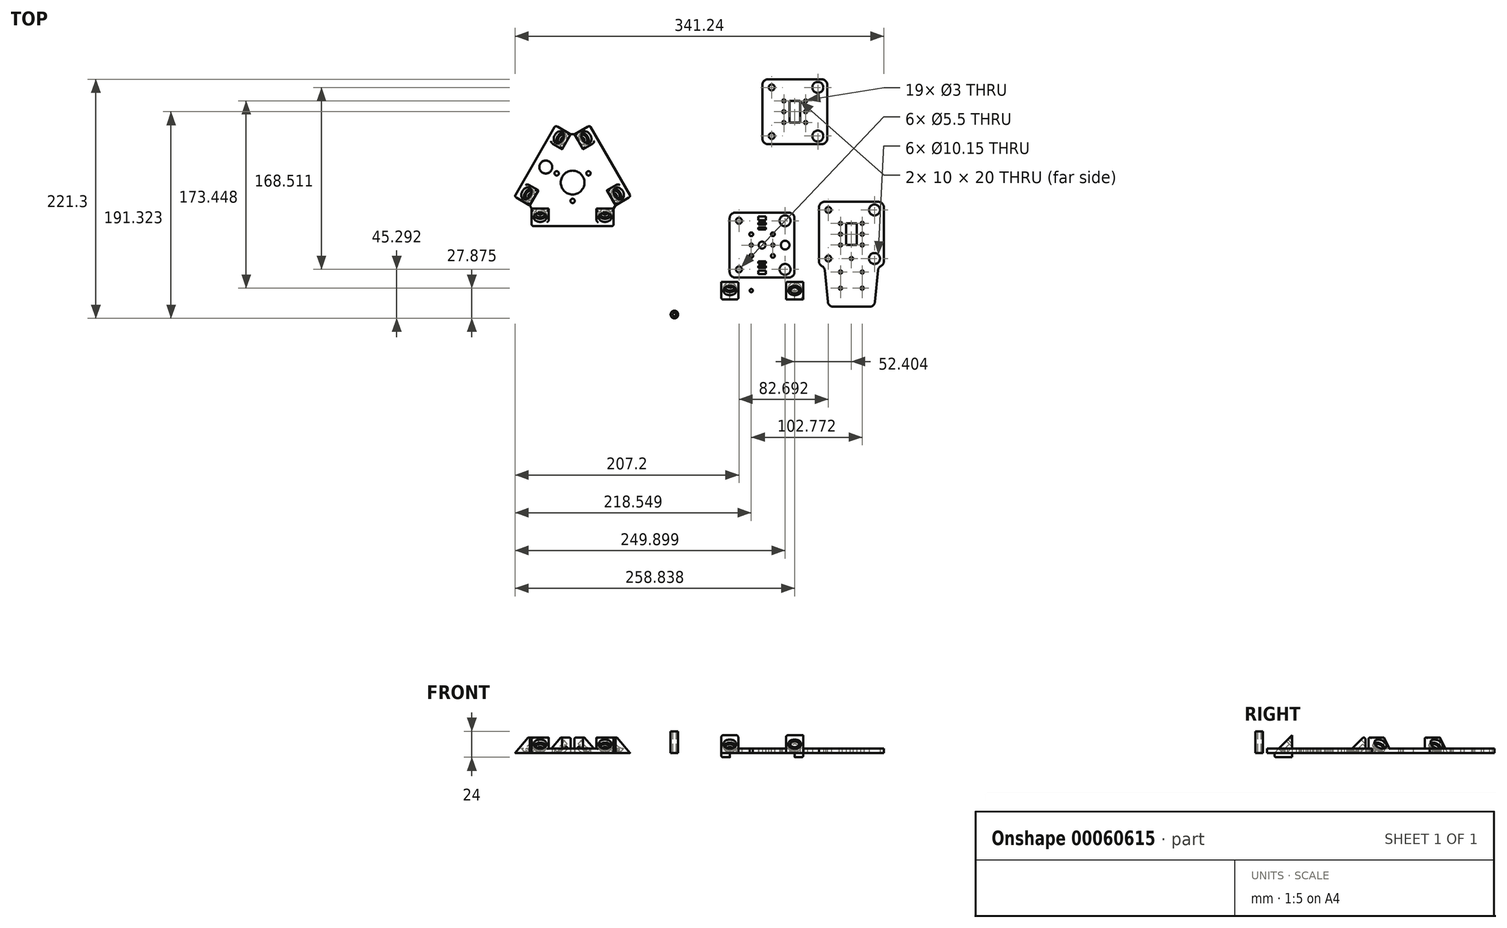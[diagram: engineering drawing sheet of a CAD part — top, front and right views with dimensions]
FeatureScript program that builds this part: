
annotation { "Feature Type Name" : "Feature", "Feature Type Description" : "" }
export const myFeature = defineFeature(function(context is Context, id is Id, definition is map)
    precondition{}
    {
        {
            var Q0;
            Q0=qCreatedBy(makeId("Top.planeOp"),FACE);
            var sketch = newSketch(context, id + "F0", { "sketchPlane" : qUnion([Q0])});
            skArc(sketch, "E0", {"start": v(24.79, -19.87) * mm, "mid": v(28.33, -18.4) * mm, "end": v(29.79, -14.87) * mm});
            skLineSegment(sketch, "E1", {"start": v(24.79, -19.87) * mm, "end": v(-25.21, -19.87) * mm});
            skArc(sketch, "E2", {"start": v(29.79, 35.13) * mm, "mid": v(28.33, 38.67) * mm, "end": v(24.79, 40.13) * mm});
            skLineSegment(sketch, "E3", {"start": v(29.79, 35.13) * mm, "end": v(29.79, -14.87) * mm});
            skArc(sketch, "E4", {"start": v(-25.21, 40.13) * mm, "mid": v(-28.75, 38.67) * mm, "end": v(-30.21, 35.13) * mm});
            skLineSegment(sketch, "E5", {"start": v(-25.21, 40.13) * mm, "end": v(24.79, 40.13) * mm});
            skArc(sketch, "E6", {"start": v(-30.21, -14.87) * mm, "mid": v(-28.75, -18.4) * mm, "end": v(-25.21, -19.87) * mm});
            skLineSegment(sketch, "E7", {"start": v(-30.21, -14.87) * mm, "end": v(-30.21, 35.13) * mm});
            skCircle(sketch, "E8", {"center": v(30, -32.16) * mm, "radius": 5.9 * mm, "construction": true});
            skCircle(sketch, "E9", {"center": v(-30, -32.16) * mm, "radius": 5.9 * mm, "construction": true});
            skLineSegment(sketch, "E10", {"start": v(-30.85, -40.13) * mm, "end": v(30.85, -40.13) * mm});
            skLineSegment(sketch, "E11", {"start": v(30.85, -23.83) * mm, "end": v(-30.85, -23.83) * mm});
            skCircle(sketch, "E12", {"center": v(21.14, 32.63) * mm, "radius": 5.08 * mm});
            skCircle(sketch, "E13", {"center": v(21.14, -12.37) * mm, "radius": 5.08 * mm});
            skCircle(sketch, "E14", {"center": v(-21.56, 32.63) * mm, "radius": 2.75 * mm});
            skCircle(sketch, "E15", {"center": v(-21.56, -12.37) * mm, "radius": 2.75 * mm});
            skCircle(sketch, "E16", {"center": v(-10.21, 20.13) * mm, "radius": 1.75 * mm});
            skCircle(sketch, "E17", {"center": v(-10.21, 0.13) * mm, "radius": 1.75 * mm});
            skCircle(sketch, "E18", {"center": v(9.79, 0.13) * mm, "radius": 1.75 * mm});
            skCircle(sketch, "E19", {"center": v(9.79, 20.13) * mm, "radius": 1.75 * mm});
            skLineSegment(sketch, "E20", {"start": v(-3.63, -6.88) * mm, "end": v(3.37, -6.88) * mm});
            skLineSegment(sketch, "E21", {"start": v(3.37, -6.88) * mm, "end": v(3.37, -4.88) * mm});
            skLineSegment(sketch, "E22", {"start": v(3.37, -4.88) * mm, "end": v(-3.63, -4.88) * mm});
            skLineSegment(sketch, "E23", {"start": v(-3.63, -4.88) * mm, "end": v(-3.63, -6.88) * mm});
            skLineSegment(sketch, "E24", {"start": v(-3.66, -11.08) * mm, "end": v(3.34, -11.08) * mm});
            skLineSegment(sketch, "E25", {"start": v(3.34, -11.08) * mm, "end": v(3.34, -9.08) * mm});
            skLineSegment(sketch, "E26", {"start": v(3.34, -9.08) * mm, "end": v(-3.66, -9.08) * mm});
            skLineSegment(sketch, "E27", {"start": v(-3.66, -9.08) * mm, "end": v(-3.66, -11.08) * mm});
            skLineSegment(sketch, "E28", {"start": v(3.35, -16.82) * mm, "end": v(3.35, -13.38) * mm});
            skLineSegment(sketch, "E29", {"start": v(3.35, -13.38) * mm, "end": v(-3.63, -13.38) * mm});
            skLineSegment(sketch, "E30", {"start": v(-3.63, 33.12) * mm, "end": v(3.37, 33.12) * mm});
            skLineSegment(sketch, "E31", {"start": v(3.37, 33.12) * mm, "end": v(3.37, 36.53) * mm});
            skLineSegment(sketch, "E32", {"start": v(3.37, 36.53) * mm, "end": v(-3.63, 36.52) * mm});
            skLineSegment(sketch, "E33", {"start": v(-3.63, 36.52) * mm, "end": v(-3.63, 33.12) * mm});
            skLineSegment(sketch, "E34", {"start": v(-3.66, 28.92) * mm, "end": v(3.34, 28.92) * mm});
            skLineSegment(sketch, "E35", {"start": v(3.34, 28.92) * mm, "end": v(3.34, 30.92) * mm});
            skLineSegment(sketch, "E36", {"start": v(3.34, 30.92) * mm, "end": v(-3.66, 30.92) * mm});
            skLineSegment(sketch, "E37", {"start": v(-3.66, 30.92) * mm, "end": v(-3.66, 28.92) * mm});
            skLineSegment(sketch, "E38", {"start": v(-3.63, 24.62) * mm, "end": v(3.37, 24.62) * mm});
            skLineSegment(sketch, "E39", {"start": v(3.37, 24.62) * mm, "end": v(3.37, 26.62) * mm});
            skLineSegment(sketch, "E40", {"start": v(3.37, 26.62) * mm, "end": v(-3.63, 26.62) * mm});
            skLineSegment(sketch, "E41", {"start": v(-3.63, 26.62) * mm, "end": v(-3.63, 24.62) * mm});
            skCircle(sketch, "E42", {"center": v(-10.21, 10.13) * mm, "radius": 1.5 * mm});
            skCircle(sketch, "E43", {"center": v(9.79, 10.13) * mm, "radius": 1.5 * mm});
            skCircle(sketch, "E44", {"center": v(-10.18, -31.98) * mm, "radius": 1.5 * mm});
            skCircle(sketch, "E45", {"center": v(9.82, -31.98) * mm, "radius": 1.5 * mm});
            skCircle(sketch, "E46", {"center": v(-0.21, 10.13) * mm, "radius": 3.2 * mm});
            skPoint(sketch, "E47", {"position": v(-3.63, 36.52) * mm});
            skLineSegment(sketch, "E48", {"start": v(-3.63, -16.82) * mm, "end": v(3.35, -16.82) * mm});
            skLineSegment(sketch, "E49", {"start": v(-3.63, -16.82) * mm, "end": v(-3.63, -13.38) * mm});
            skCircle(sketch, "E50", {"center": v(21.14, 10.13) * mm, "radius": 4 * mm});
            skLineSegment(sketch, "E51", {"start": v(112.48, 45.2) * mm, "end": v(112.48, -4.8) * mm});
            skLineSegment(sketch, "E52", {"start": v(57.48, 50.2) * mm, "end": v(107.48, 50.2) * mm});
            skLineSegment(sketch, "E53", {"start": v(52.48, -4.8) * mm, "end": v(52.48, 45.2) * mm});
            skCircle(sketch, "E54", {"center": v(103.83, 42.7) * mm, "radius": 5.08 * mm});
            skCircle(sketch, "E55", {"center": v(103.83, -2.3) * mm, "radius": 5.08 * mm});
            skCircle(sketch, "E56", {"center": v(61.13, -2.3) * mm, "radius": 2.75 * mm});
            skCircle(sketch, "E57", {"center": v(61.13, 42.7) * mm, "radius": 2.75 * mm});
            skArc(sketch, "E58", {"start": v(109.8, -9.23) * mm, "mid": v(111.76, -7.4) * mm, "end": v(112.48, -4.8) * mm});
            skArc(sketch, "E59", {"start": v(112.48, 45.2) * mm, "mid": v(111.02, 48.73) * mm, "end": v(107.48, 50.2) * mm});
            skArc(sketch, "E60", {"start": v(57.48, 50.2) * mm, "mid": v(53.95, 48.73) * mm, "end": v(52.48, 45.2) * mm});
            skArc(sketch, "E61", {"start": v(52.48, -4.8) * mm, "mid": v(53.95, -8.34) * mm, "end": v(57.48, -9.8) * mm});
            skLineSegment(sketch, "E62", {"start": v(82.48, -47) * mm, "end": v(82.48, -9.8) * mm, "construction": true});
            skLineSegment(sketch, "E63", {"start": v(82.48, -47) * mm, "end": v(99.3, -47) * mm});
            skLineSegment(sketch, "E64", {"start": v(107.15, -13.17) * mm, "end": v(104.27, -42.49) * mm});
            skPoint(sketch, "E65.visualSharp", {"position": v(107.48, -9.8) * mm});
            skArc(sketch, "E65.filletArc", {"start": v(109.8, -9.23) * mm, "mid": v(107.98, -10.87) * mm, "end": v(107.15, -13.17) * mm});
            skPoint(sketch, "E66.visualSharp", {"position": v(103.83, -47) * mm});
            skArc(sketch, "E66.filletArc", {"start": v(99.3, -47) * mm, "mid": v(102.66, -45.7) * mm, "end": v(104.27, -42.49) * mm});
            skLineSegment(sketch, "E67.MirrorCS", {"start": v(82.48, -47) * mm, "end": v(65.66, -47) * mm});
            skArc(sketch, "E68.MirrorCS", {"start": v(65.66, -47) * mm, "mid": v(62.3, -45.7) * mm, "end": v(60.69, -42.49) * mm});
            skLineSegment(sketch, "E69.MirrorCS", {"start": v(57.81, -13.17) * mm, "end": v(60.69, -42.49) * mm});
            skArc(sketch, "E70.MirrorCS", {"start": v(55.16, -9.23) * mm, "mid": v(56.98, -10.87) * mm, "end": v(57.81, -13.17) * mm});
            skLineSegment(sketch, "E71", {"start": v(82.48, 30.21) * mm, "end": v(87.48, 30.21) * mm});
            skLineSegment(sketch, "E72.bottom", {"start": v(87.48, 30.21) * mm, "end": v(77.48, 30.21) * mm});
            skLineSegment(sketch, "E72.left", {"start": v(87.48, 30.21) * mm, "end": v(87.48, 10.21) * mm});
            skLineSegment(sketch, "E72.right", {"start": v(77.48, 30.21) * mm, "end": v(77.48, 10.21) * mm});
            skLineSegment(sketch, "E73", {"start": v(92.56, 30.21) * mm, "end": v(92.56, 10.21) * mm, "construction": true});
            skLineSegment(sketch, "E74", {"start": v(87.48, 10.21) * mm, "end": v(77.48, 10.21) * mm});
            skCircle(sketch, "E75", {"center": v(92.56, 30.21) * mm, "radius": 1.5 * mm});
            skCircle(sketch, "E76", {"center": v(92.56, 20.21) * mm, "radius": 1.5 * mm});
            skCircle(sketch, "E77", {"center": v(92.56, 10.21) * mm, "radius": 1.5 * mm});
            skLineSegment(sketch, "E78", {"start": v(92.56, 10.21) * mm, "end": v(92.56, -14.79) * mm, "construction": true});
            skLineSegment(sketch, "E79", {"start": v(92.56, -14.79) * mm, "end": v(92.56, -29.79) * mm, "construction": true});
            skCircle(sketch, "E80", {"center": v(92.56, -14.79) * mm, "radius": 1.5 * mm});
            skCircle(sketch, "E81", {"center": v(92.56, -29.79) * mm, "radius": 1.5 * mm});
            skCircle(sketch, "E82.MirrorC", {"center": v(72.4, -14.79) * mm, "radius": 1.5 * mm});
            skCircle(sketch, "E83.MirrorC", {"center": v(72.4, -29.79) * mm, "radius": 1.5 * mm});
            skCircle(sketch, "E84.MirrorC", {"center": v(72.4, 10.21) * mm, "radius": 1.5 * mm});
            skCircle(sketch, "E85.MirrorC", {"center": v(72.4, 20.21) * mm, "radius": 1.5 * mm});
            skCircle(sketch, "E86.MirrorC", {"center": v(72.4, 30.21) * mm, "radius": 1.5 * mm});
            skLineSegment(sketch, "E87", {"start": v(60.08, 158.64) * mm, "end": v(60.08, 108.64) * mm});
            skLineSegment(sketch, "E88", {"start": v(5.08, 163.64) * mm, "end": v(55.08, 163.64) * mm});
            skLineSegment(sketch, "E89", {"start": v(0.08, 108.64) * mm, "end": v(0.08, 158.64) * mm});
            skCircle(sketch, "E90", {"center": v(51.43, 156.14) * mm, "radius": 5.08 * mm});
            skPoint(sketch, "E91.visualSharp", {"position": v(55.08, 103.64) * mm});
            skLineSegment(sketch, "E92.right", {"start": v(25.08, 143.66) * mm, "end": v(25.08, 123.66) * mm});
            skLineSegment(sketch, "E92.left", {"start": v(35.08, 143.66) * mm, "end": v(35.08, 123.66) * mm});
            skLineSegment(sketch, "E93", {"start": v(40.16, 143.66) * mm, "end": v(40.16, 123.66) * mm, "construction": true});
            skCircle(sketch, "E94", {"center": v(51.43, 111.14) * mm, "radius": 5.08 * mm});
            skCircle(sketch, "E95.MirrorC", {"center": v(20, 133.66) * mm, "radius": 1.5 * mm});
            skCircle(sketch, "E96", {"center": v(8.73, 111.14) * mm, "radius": 2.75 * mm});
            skCircle(sketch, "E97.MirrorC", {"center": v(20, 143.66) * mm, "radius": 1.5 * mm});
            skCircle(sketch, "E98", {"center": v(8.73, 156.14) * mm, "radius": 2.75 * mm});
            skCircle(sketch, "E99", {"center": v(40.16, 133.66) * mm, "radius": 1.5 * mm});
            skCircle(sketch, "E100.MirrorC", {"center": v(20, 123.66) * mm, "radius": 1.5 * mm});
            skLineSegment(sketch, "E92.bottom", {"start": v(35.08, 143.66) * mm, "end": v(25.08, 143.66) * mm});
            skArc(sketch, "E101", {"start": v(60.08, 158.64) * mm, "mid": v(58.61, 162.18) * mm, "end": v(55.08, 163.64) * mm});
            skLineSegment(sketch, "E102", {"start": v(35.08, 123.66) * mm, "end": v(25.08, 123.66) * mm});
            skArc(sketch, "E103", {"start": v(5.08, 163.64) * mm, "mid": v(1.54, 162.18) * mm, "end": v(0.08, 158.64) * mm});
            skCircle(sketch, "E104", {"center": v(40.16, 143.66) * mm, "radius": 1.5 * mm});
            skArc(sketch, "E105", {"start": v(0.08, 108.64) * mm, "mid": v(1.54, 105.1) * mm, "end": v(5.08, 103.64) * mm});
            skLineSegment(sketch, "E106", {"start": v(30.08, 143.66) * mm, "end": v(35.08, 143.66) * mm});
            skLineSegment(sketch, "E107", {"start": v(5.08, 103.64) * mm, "end": v(55.08, 103.64) * mm});
            skLineSegment(sketch, "E108", {"start": v(60.08, 108.64) * mm, "end": v(60.08, 108.64) * mm});
            skPoint(sketch, "E109.visualSharp", {"position": v(60.08, 103.64) * mm});
            skArc(sketch, "E109.filletArc", {"start": v(55.08, 103.64) * mm, "mid": v(58.61, 105.1) * mm, "end": v(60.08, 108.64) * mm});
            skCircle(sketch, "E110.MirrorC", {"center": v(40.16, 123.66) * mm, "radius": 1.5 * mm});
            skCircle(sketch, "E111", {"center": v(135.68, 118.4) * mm, "radius": 24 * mm});
            skCircle(sketch, "E112", {"center": v(135.68, 118.4) * mm, "radius": 7.5 * mm});
            skLineSegment(sketch, "E113", {"start": v(61.13, -2.3) * mm, "end": v(103.83, -2.3) * mm, "construction": true});
            skCircle(sketch, "E114", {"center": v(82.48, -2.3) * mm, "radius": 1.5 * mm});
            skArc(sketch, "E115.MirrorCS", {"start": v(112.48, -4.8) * mm, "mid": v(111.02, -8.34) * mm, "end": v(107.48, -9.8) * mm});
            skLineSegment(sketch, "E116", {"start": v(57.48, -9.8) * mm, "end": v(107.48, -9.8) * mm, "construction": true});
            skLineSegment(sketch, "E117.bottom", {"start": v(-30.85, -40.13) * mm, "end": v(-37.97, -40.13) * mm});
            skLineSegment(sketch, "E117.top", {"start": v(-30.85, -23.83) * mm, "end": v(-37.97, -23.83) * mm});
            skLineSegment(sketch, "E117.right", {"start": v(-37.97, -40.13) * mm, "end": v(-37.97, -23.83) * mm});
            skLineSegment(sketch, "E118", {"start": v(0, -40.13) * mm, "end": v(0, -23.83) * mm, "construction": true});
            skLineSegment(sketch, "E119.MirrorCS", {"start": v(30.85, -40.13) * mm, "end": v(37.97, -40.13) * mm});
            skLineSegment(sketch, "E120.MirrorCS", {"start": v(37.97, -40.13) * mm, "end": v(37.97, -23.83) * mm});
            skLineSegment(sketch, "E121.MirrorCS", {"start": v(30.85, -23.83) * mm, "end": v(37.97, -23.83) * mm});
            skLineSegment(sketch, "E122", {"start": v(-30, -32.16) * mm, "end": v(-30, -57.06) * mm, "construction": true});
            skLineSegment(sketch, "E123.MirrorCS", {"start": v(-22.03, -40.13) * mm, "end": v(-22.03, -23.83) * mm});
            skLineSegment(sketch, "E124", {"start": v(30, -32.16) * mm, "end": v(30, -52.4) * mm, "construction": true});
            skLineSegment(sketch, "E125.MirrorCS", {"start": v(22.03, -40.13) * mm, "end": v(22.03, -23.83) * mm});
            skLineSegment(sketch, "E126", {"start": v(-30, -40.13) * mm, "end": v(-30, -23.83) * mm});
            skLineSegment(sketch, "E127", {"start": v(30, -40.13) * mm, "end": v(30, -23.83) * mm});
            skSolve(sketch);
        }
        {
            var Q0;
            Q0=qCreatedBy(makeId("Top.planeOp"),FACE);
            var sketch = newSketch(context, id + "F1", { "sketchPlane" : qUnion([Q0])});
            skLineSegment(sketch, "E128", {"start": v(-206.4, 27.73) * mm, "end": v(-144.7, 27.73) * mm});
            skLineSegment(sketch, "E129", {"start": v(-144.7, 44.03) * mm, "end": v(-153.53, 44.03) * mm});
            skLineSegment(sketch, "E130.bottom", {"start": v(-206.4, 27.73) * mm, "end": v(-213.53, 27.73) * mm});
            skLineSegment(sketch, "E130.top", {"start": v(-206.4, 44.03) * mm, "end": v(-213.53, 44.03) * mm});
            skLineSegment(sketch, "E130.right", {"start": v(-213.53, 27.73) * mm, "end": v(-213.53, 44.03) * mm});
            skLineSegment(sketch, "E131", {"start": v(-175.56, 27.73) * mm, "end": v(-175.56, 44.03) * mm, "construction": true});
            skLineSegment(sketch, "E132.MirrorCS", {"start": v(-144.7, 27.73) * mm, "end": v(-137.59, 27.73) * mm});
            skLineSegment(sketch, "E133.MirrorCS", {"start": v(-137.59, 27.73) * mm, "end": v(-137.59, 44.03) * mm});
            skLineSegment(sketch, "E134.MirrorCS", {"start": v(-144.7, 44.03) * mm, "end": v(-137.59, 44.03) * mm});
            skLineSegment(sketch, "E135", {"start": v(-205.56, 35.7) * mm, "end": v(-205.56, 10.8) * mm, "construction": true});
            skLineSegment(sketch, "E136.MirrorCS", {"start": v(-197.59, 27.73) * mm, "end": v(-197.59, 44.03) * mm});
            skLineSegment(sketch, "E137", {"start": v(-145.56, 35.7) * mm, "end": v(-145.56, 15.46) * mm, "construction": true});
            skLineSegment(sketch, "E138.MirrorCS", {"start": v(-153.53, 27.73) * mm, "end": v(-153.53, 44.03) * mm});
            skLineSegment(sketch, "E139", {"start": v(-175.56, 44.03) * mm, "end": v(-175.56, 104.1) * mm, "construction": true});
            skLineSegment(sketch, "E140.1.0", {"start": v(-121.75, 55.16) * mm, "end": v(-135.87, 47.01) * mm});
            skLineSegment(sketch, "E140.1.1", {"start": v(-129.72, 68.97) * mm, "end": v(-143.84, 60.82) * mm});
            skLineSegment(sketch, "E140.1.2", {"start": v(-151.75, 107.12) * mm, "end": v(-165.87, 98.97) * mm});
            skLineSegment(sketch, "E140.1.3", {"start": v(-155.86, 79.43) * mm, "end": v(-207.88, 49.4) * mm, "construction": true});
            skLineSegment(sketch, "E140.1.4", {"start": v(-141.74, 87.58) * mm, "end": v(-155.86, 79.43) * mm, "construction": true});
            skLineSegment(sketch, "E140.1.5", {"start": v(-159.72, 120.93) * mm, "end": v(-173.84, 112.78) * mm});
            skLineSegment(sketch, "E140.1.6", {"start": v(-125.3, 61.33) * mm, "end": v(-156.16, 114.76) * mm});
            skLineSegment(sketch, "E140.1.7", {"start": v(-162.64, 110.04) * mm, "end": v(-145.1, 120.16) * mm, "construction": true});
            skLineSegment(sketch, "E140.1.8", {"start": v(-132.64, 58.08) * mm, "end": v(-111.08, 70.53) * mm, "construction": true});
            skLineSegment(sketch, "E140.1.9", {"start": v(-170.28, 106.61) * mm, "end": v(-165.87, 98.97) * mm});
            skLineSegment(sketch, "E140.1.12", {"start": v(-139.43, 53.18) * mm, "end": v(-135.87, 47.01) * mm});
            skLineSegment(sketch, "E140.1.13", {"start": v(-156.16, 114.76) * mm, "end": v(-159.72, 120.93) * mm});
            skLineSegment(sketch, "E140.1.14", {"start": v(-125.3, 61.33) * mm, "end": v(-121.75, 55.16) * mm});
            skLineSegment(sketch, "E140.1.15", {"start": v(-170.28, 106.61) * mm, "end": v(-173.84, 112.78) * mm});
            skLineSegment(sketch, "E140.2.0", {"start": v(-191.4, 120.93) * mm, "end": v(-177.28, 112.78) * mm});
            skLineSegment(sketch, "E140.2.1", {"start": v(-199.36, 107.12) * mm, "end": v(-185.25, 98.97) * mm});
            skLineSegment(sketch, "E140.2.2", {"start": v(-221.4, 68.97) * mm, "end": v(-207.28, 60.82) * mm});
            skLineSegment(sketch, "E140.2.3", {"start": v(-196.02, 79.88) * mm, "end": v(-144, 49.84) * mm, "construction": true});
            skLineSegment(sketch, "E140.2.4", {"start": v(-210.14, 88.03) * mm, "end": v(-196.02, 79.88) * mm, "construction": true});
            skLineSegment(sketch, "E140.2.5", {"start": v(-229.36, 55.16) * mm, "end": v(-215.25, 47.01) * mm});
            skLineSegment(sketch, "E140.2.6", {"start": v(-194.95, 114.76) * mm, "end": v(-225.8, 61.33) * mm});
            skLineSegment(sketch, "E140.2.7", {"start": v(-218.47, 58.08) * mm, "end": v(-236, 68.2) * mm, "construction": true});
            skLineSegment(sketch, "E140.2.8", {"start": v(-188.47, 110.04) * mm, "end": v(-210.04, 122.49) * mm, "construction": true});
            skLineSegment(sketch, "E140.2.9", {"start": v(-211.69, 53.18) * mm, "end": v(-207.28, 60.82) * mm});
            skLineSegment(sketch, "E140.2.12", {"start": v(-180.84, 106.61) * mm, "end": v(-177.28, 112.78) * mm});
            skLineSegment(sketch, "E140.2.13", {"start": v(-225.8, 61.33) * mm, "end": v(-229.36, 55.16) * mm});
            skLineSegment(sketch, "E140.2.14", {"start": v(-194.95, 114.76) * mm, "end": v(-191.4, 120.93) * mm});
            skLineSegment(sketch, "E140.2.15", {"start": v(-211.69, 53.18) * mm, "end": v(-215.25, 47.01) * mm});
            skPoint(sketch, "E140.center", {"position": v(-175.56, 68.06) * mm});
            skLineSegment(sketch, "E141", {"start": v(-215.25, 47.01) * mm, "end": v(-213.53, 44.03) * mm});
            skLineSegment(sketch, "E142", {"start": v(-135.87, 47.01) * mm, "end": v(-137.59, 44.03) * mm});
            skLineSegment(sketch, "E143", {"start": v(-177.28, 112.78) * mm, "end": v(-173.84, 112.78) * mm});
            skCircle(sketch, "E144", {"center": v(-175.56, 68.06) * mm, "radius": 11 * mm});
            skCircle(sketch, "E145", {"center": v(-190.28, 76.56) * mm, "radius": 2 * mm});
            skCircle(sketch, "E146", {"center": v(-160.83, 76.56) * mm, "radius": 2 * mm});
            skCircle(sketch, "E147", {"center": v(-175.56, 51.06) * mm, "radius": 2 * mm});
            skLineSegment(sketch, "E148.trimOffspring", {"start": v(-185.25, 98.97) * mm, "end": v(-180.84, 106.61) * mm});
            skLineSegment(sketch, "E149.trimOffspring", {"start": v(-143.84, 60.82) * mm, "end": v(-139.43, 53.18) * mm});
            skLineSegment(sketch, "E150.trimOffspring", {"start": v(-197.59, 44.03) * mm, "end": v(-206.4, 44.03) * mm});
            skCircle(sketch, "E151", {"center": v(-200.38, 82.4) * mm, "radius": 6 * mm});
            skSolve(sketch);
        }
        {
            var Q0;
            Q0=makeQuery(id+"F0.imprint","IMPRINT",FACE,{"disambiguationData":[TD([[makeQuery(id+"F0.imprint","IMPRINT",EDGE,{"derivedFrom":sQuery(id+"F0.wireOp",EDGE,"E0")}),1.0]])]});
            var Q1;
            Q1=makeQuery(id+"F0.imprint","IMPRINT",FACE,{"disambiguationData":[TD([[makeQuery(id+"F0.imprint","IMPRINT",EDGE,{"derivedFrom":sQuery(id+"F0.wireOp",EDGE,"f96d0108-ce3c-40f9-9041-a5f02a56c2c8")}),-1.0]])]});
            var Q2;
            Q2=makeQuery(id+"F0.imprint","IMPRINT",FACE,{"disambiguationData":[TD([[makeQuery(id+"F0.imprint","IMPRINT",EDGE,{"derivedFrom":sQuery(id+"F0.wireOp",EDGE,"fc6a74a1-8ae2-464b-8a54-e97a179053b1")}),1.0]])]});
            var Q3;
            Q3=makeQuery(id+"F0.imprint","IMPRINT",FACE,{"disambiguationData":[TD([[makeQuery(id+"F0.imprint","IMPRINT",EDGE,{"derivedFrom":sQuery(id+"F0.wireOp",EDGE,"E51")}),-1.0]])]});
            var Q4;
            Q4=makeQuery(id+"F0.imprint","IMPRINT",FACE,{"disambiguationData":[TD([[makeQuery(id+"F0.imprint","IMPRINT",EDGE,{"derivedFrom":sQuery(id+"F0.wireOp",EDGE,"E87")}),-1.0]])]});
            var Q5;
            Q5=makeQuery(id+"F0.imprint","IMPRINT",FACE,{"disambiguationData":[TD([[makeQuery(id+"F0.imprint","IMPRINT",EDGE,{"derivedFrom":sQuery(id+"F0.wireOp",EDGE,"E44")}),1.0]])]});
            var Q6;
            {var subQ1=sQuery(id+"F1.wireOp",EDGE,"E140.2.1");Q6=makeQuery(id+"F1.imprint","IMPRINT",FACE,{"disambiguationData":[TD([[makeQuery(id+"F1.imprint","IMPRINT",EDGE,{"derivedFrom":subQ1}),-1.0]])]});}
            var Q7;
            {var subQ12=sQuery(id+"F1.wireOp",EDGE,"E130.top");Q7=makeQuery(id+"F1.imprint","IMPRINT",FACE,{"disambiguationData":[TD([[makeQuery(id+"F1.imprint","IMPRINT",EDGE,{"derivedFrom":subQ12}),-1.0]])]});}
            var Q8;
            {var subQ1=sQuery(id+"F1.wireOp",EDGE,"E140.1.1");Q8=makeQuery(id+"F1.imprint","IMPRINT",FACE,{"disambiguationData":[TD([[makeQuery(id+"F1.imprint","IMPRINT",EDGE,{"derivedFrom":subQ1}),-1.0]])]});}
            var Q9;
            Q9=makeQuery(id+"F1.imprint","IMPRINT",FACE,{"disambiguationData":[TD([[makeQuery(id+"F1.imprint","IMPRINT",EDGE,{"derivedFrom":sQuery(id+"F1.wireOp",EDGE,"f1ae98ec-eddd-4e72-9429-8ecdf1ed458a")}),1.0]])]});
            extrude(context, id + "F2", {"entities" : qUnion([Q0, Q1, Q2, Q3, Q4, Q5, Q6, Q7, Q8, Q9]), "depth" : 4 * mm});
        }
        {
            var Q0;
            Q0=makeQuery(id+"F0.imprint","IMPRINT",FACE,{"disambiguationData":[TD([[makeQuery(id+"F0.imprint","IMPRINT",EDGE,{"derivedFrom":sQuery(id+"F0.wireOp",EDGE,"E9")}),-1.0]])]});
            var Q1;
            Q1=makeQuery(id+"F0.imprint","IMPRINT",FACE,{"disambiguationData":[TD([[makeQuery(id+"F0.imprint","IMPRINT",EDGE,{"derivedFrom":sQuery(id+"F0.wireOp",EDGE,"E8")}),1.0]])]});
            var Q2;
            Q2=makeQuery(id+"F0.imprint","IMPRINT",FACE,{"disambiguationData":[TD([[makeQuery(id+"F0.imprint","IMPRINT",EDGE,{"derivedFrom":sQuery(id+"F0.wireOp",EDGE,"E8")}),-1.0]])]});
            var Q3;
            Q3=makeQuery(id+"F0.imprint","IMPRINT",FACE,{"disambiguationData":[TD([[makeQuery(id+"F0.imprint","IMPRINT",EDGE,{"derivedFrom":sQuery(id+"F0.wireOp",EDGE,"E9")}),1.0]])]});
            var Q4;
            Q4=makeQuery(id+"F1.imprint","IMPRINT",FACE,{"disambiguationData":[TD([[makeQuery(id+"F1.imprint","IMPRINT",EDGE,{"derivedFrom":sQuery(id+"F1.wireOp",EDGE,"346c870d-bf97-44aa-bfb7-157ee8bb922b.2.6")}),1.0]])]});
            var Q5;
            Q5=makeQuery(id+"F1.imprint","IMPRINT",FACE,{"disambiguationData":[TD([[makeQuery(id+"F1.imprint","IMPRINT",EDGE,{"derivedFrom":sQuery(id+"F1.wireOp",EDGE,"346c870d-bf97-44aa-bfb7-157ee8bb922b.2.5")}),1.0]])]});
            var Q6;
            Q6=makeQuery(id+"F1.imprint","IMPRINT",FACE,{"disambiguationData":[TD([[makeQuery(id+"F1.imprint","IMPRINT",EDGE,{"derivedFrom":sQuery(id+"F1.wireOp",EDGE,"346c870d-bf97-44aa-bfb7-157ee8bb922b.2.5")}),-1.0]])]});
            var Q7;
            Q7=makeQuery(id+"F1.imprint","IMPRINT",FACE,{"disambiguationData":[TD([[makeQuery(id+"F1.imprint","IMPRINT",EDGE,{"derivedFrom":sQuery(id+"F1.wireOp",EDGE,"346c870d-bf97-44aa-bfb7-157ee8bb922b.2.6")}),-1.0]])]});
            var Q8;
            Q8=makeQuery(id+"F1.imprint","IMPRINT",FACE,{"disambiguationData":[TD([[makeQuery(id+"F1.imprint","IMPRINT",EDGE,{"derivedFrom":sQuery(id+"F1.wireOp",EDGE,"1521ab2a-ef47-4488-a64c-4af944e9871a")}),-1.0]])]});
            var Q9;
            Q9=makeQuery(id+"F1.imprint","IMPRINT",FACE,{"disambiguationData":[TD([[makeQuery(id+"F1.imprint","IMPRINT",EDGE,{"derivedFrom":sQuery(id+"F1.wireOp",EDGE,"1521ab2a-ef47-4488-a64c-4af944e9871a")}),1.0]])]});
            var Q10;
            Q10=makeQuery(id+"F1.imprint","IMPRINT",FACE,{"disambiguationData":[TD([[makeQuery(id+"F1.imprint","IMPRINT",EDGE,{"derivedFrom":sQuery(id+"F1.wireOp",EDGE,"f8b58d7a-966b-4f00-93db-83ad977ebcb6")}),1.0]])]});
            var Q11;
            Q11=makeQuery(id+"F1.imprint","IMPRINT",FACE,{"disambiguationData":[TD([[makeQuery(id+"F1.imprint","IMPRINT",EDGE,{"derivedFrom":sQuery(id+"F1.wireOp",EDGE,"f8b58d7a-966b-4f00-93db-83ad977ebcb6")}),-1.0]])]});
            var Q12;
            Q12=makeQuery(id+"F1.imprint","IMPRINT",FACE,{"disambiguationData":[TD([[makeQuery(id+"F1.imprint","IMPRINT",EDGE,{"derivedFrom":sQuery(id+"F1.wireOp",EDGE,"346c870d-bf97-44aa-bfb7-157ee8bb922b.1.5")}),1.0]])]});
            var Q13;
            Q13=makeQuery(id+"F1.imprint","IMPRINT",FACE,{"disambiguationData":[TD([[makeQuery(id+"F1.imprint","IMPRINT",EDGE,{"derivedFrom":sQuery(id+"F1.wireOp",EDGE,"346c870d-bf97-44aa-bfb7-157ee8bb922b.1.5")}),-1.0]])]});
            var Q14;
            Q14=makeQuery(id+"F1.imprint","IMPRINT",FACE,{"disambiguationData":[TD([[makeQuery(id+"F1.imprint","IMPRINT",EDGE,{"derivedFrom":sQuery(id+"F1.wireOp",EDGE,"346c870d-bf97-44aa-bfb7-157ee8bb922b.1.6")}),1.0]])]});
            var Q15;
            Q15=makeQuery(id+"F1.imprint","IMPRINT",FACE,{"disambiguationData":[TD([[makeQuery(id+"F1.imprint","IMPRINT",EDGE,{"derivedFrom":sQuery(id+"F1.wireOp",EDGE,"346c870d-bf97-44aa-bfb7-157ee8bb922b.1.6")}),-1.0]])]});
            var Q16;
            {var subQ1=sQuery(id+"F1.wireOp",EDGE,"E130.bottom");Q16=makeQuery(id+"F1.imprint","IMPRINT",FACE,{"disambiguationData":[TD([[makeQuery(id+"F1.imprint","IMPRINT",EDGE,{"derivedFrom":subQ1}),-1.0]])]});}
            var Q17;
            {var subQ1=sQuery(id+"F1.wireOp",EDGE,"E140.2.2");Q17=makeQuery(id+"F1.imprint","IMPRINT",FACE,{"disambiguationData":[TD([[makeQuery(id+"F1.imprint","IMPRINT",EDGE,{"derivedFrom":subQ1}),-1.0]])]});}
            var Q18;
            Q18=makeQuery(id+"F1.imprint","IMPRINT",FACE,{"disambiguationData":[TD([[makeQuery(id+"F1.imprint","IMPRINT",EDGE,{"derivedFrom":sQuery(id+"F1.wireOp",EDGE,"E140.2.0")}),-1.0]])]});
            var Q19;
            {var subQ1=sQuery(id+"F1.wireOp",EDGE,"E140.1.2");Q19=makeQuery(id+"F1.imprint","IMPRINT",FACE,{"disambiguationData":[TD([[makeQuery(id+"F1.imprint","IMPRINT",EDGE,{"derivedFrom":subQ1}),-1.0]])]});}
            var Q20;
            Q20=makeQuery(id+"F1.imprint","IMPRINT",FACE,{"disambiguationData":[TD([[makeQuery(id+"F1.imprint","IMPRINT",EDGE,{"derivedFrom":sQuery(id+"F1.wireOp",EDGE,"E140.1.0")}),-1.0]])]});
            var Q21;
            {var subQ0=sQuery(id+"F1.wireOp",EDGE,"E132.MirrorCS");Q21=makeQuery(id+"F1.imprint","IMPRINT",FACE,{"disambiguationData":[TD([[makeQuery(id+"F1.imprint","IMPRINT",EDGE,{"derivedFrom":subQ0}),1.0]])]});}
            var Q22;
            {var subQ0=sQuery(id+"F0.wireOp",EDGE,"E123.MirrorCS");Q22=makeQuery(id+"F0.imprint","IMPRINT",FACE,{"disambiguationData":[TD([[makeQuery(id+"F0.imprint","IMPRINT",EDGE,{"derivedFrom":subQ0}),1.0]])]});}
            var Q23;
            {var subQ1=sQuery(id+"F0.wireOp",EDGE,"E117.bottom");Q23=makeQuery(id+"F0.imprint","IMPRINT",FACE,{"disambiguationData":[TD([[makeQuery(id+"F0.imprint","IMPRINT",EDGE,{"derivedFrom":subQ1}),-1.0]])]});}
            var Q24;
            {var subQ0=sQuery(id+"F0.wireOp",EDGE,"E125.MirrorCS");Q24=makeQuery(id+"F0.imprint","IMPRINT",FACE,{"disambiguationData":[TD([[makeQuery(id+"F0.imprint","IMPRINT",EDGE,{"derivedFrom":subQ0}),-1.0]])]});}
            var Q25;
            {var subQ0=sQuery(id+"F0.wireOp",EDGE,"E119.MirrorCS");Q25=makeQuery(id+"F0.imprint","IMPRINT",FACE,{"disambiguationData":[TD([[makeQuery(id+"F0.imprint","IMPRINT",EDGE,{"derivedFrom":subQ0}),1.0]])]});}
            extrude(context, id + "F3", {"entities" : qUnion([Q0, Q1, Q2, Q3, Q4, Q5, Q6, Q7, Q8, Q9, Q10, Q11, Q12, Q13, Q14, Q15, Q16, Q17, Q18, Q19, Q20, Q21, Q22, Q23, Q24, Q25]), "operationType" : NewBodyOperationType.ADD, "depth" : 16.3 * mm});
        }
        {
            var Q0;
            {var subQ0=sQuery(id+"F0.wireOp",EDGE,"E119.MirrorCS");Q0=makeQuery(id+"F0.imprint","IMPRINT",FACE,{"disambiguationData":[TD([[makeQuery(id+"F0.imprint","IMPRINT",EDGE,{"derivedFrom":subQ0}),1.0]])]});}
            var Q1;
            {var subQ1=sQuery(id+"F0.wireOp",EDGE,"E117.bottom");Q1=makeQuery(id+"F0.imprint","IMPRINT",FACE,{"disambiguationData":[TD([[makeQuery(id+"F0.imprint","IMPRINT",EDGE,{"derivedFrom":subQ1}),-1.0]])]});}
            extrude(context, id + "F4", {"entities" : qUnion([Q0, Q1]), "operationType" : NewBodyOperationType.ADD, "oppositeDirection" : true, "depth" : 4 * mm});
        }
        {
            var Q0;
            Q0=makeQuery(id+"F3.opExtrude","CAP_EDGE",EDGE,{"disambiguationData":[OSD([sQuery(id+"F0.wireOp",EDGE,"E10"),sQuery(id+"F0.wireOp",EDGE,"E117.bottom")])],"isStart":false});
            var Q1;
            Q1=makeQuery(id+"F3.opExtrude","CAP_EDGE",EDGE,{"disambiguationData":[OSD([sQuery(id+"F0.wireOp",EDGE,"E10"),sQuery(id+"F0.wireOp",EDGE,"E119.MirrorCS")])],"isStart":false});
            var Q2;
            Q2=makeQuery(id+"F3.opExtrude","CAP_EDGE",EDGE,{"disambiguationData":[OSD([sQuery(id+"F1.wireOp",EDGE,"E140.2.6"),sQuery(id+"F1.wireOp",EDGE,"E140.2.13")])],"isStart":false});
            var Q3;
            Q3=makeQuery(id+"F3.opExtrude","CAP_EDGE",EDGE,{"disambiguationData":[OSD([sQuery(id+"F1.wireOp",EDGE,"E140.1.6"),sQuery(id+"F1.wireOp",EDGE,"E140.1.13")])],"isStart":false});
            var Q4;
            Q4=makeQuery(id+"F3.opExtrude","CAP_EDGE",EDGE,{"disambiguationData":[OSD([sQuery(id+"F1.wireOp",EDGE,"E128"),sQuery(id+"F1.wireOp",EDGE,"E132.MirrorCS")])],"isStart":false});
            chamfer(context, id + "F5", {"entities" : qUnion([Q0, Q1, Q2, Q3, Q4]), "width" : 16.3 * mm, "tangentPropagation" : true});
        }
        {
            var Q0;
            Q0=makeQuery(id+"F5.opChamfer","BLEND_FACE",FACE,{"disambiguationData":[OSD([sQuery(id+"F0.wireOp",EDGE,"E10"),sQuery(id+"F0.wireOp",EDGE,"E117.bottom")])]});
            var sketch = newSketch(context, id + "F6", { "sketchPlane" : qUnion([Q0])});
            skLineSegment(sketch, "E152", {"start": v(-22.03, -5.33) * mm, "end": v(-37.97, -28.38) * mm, "construction": true});
            skLineSegment(sketch, "E153", {"start": v(-37.97, -28.38) * mm, "end": v(22.03, -5.33) * mm, "construction": true});
            skLineSegment(sketch, "E154", {"start": v(22.03, -5.33) * mm, "end": v(37.97, -28.38) * mm, "construction": true});
            skCircle(sketch, "E155", {"center": v(30, -16.85) * mm, "radius": 6 * mm});
            skCircle(sketch, "E156", {"center": v(-30, -16.85) * mm, "radius": 6 * mm});
            skCircle(sketch, "E157", {"center": v(-30, -16.85) * mm, "radius": 4 * mm});
            skCircle(sketch, "E158", {"center": v(30, -16.85) * mm, "radius": 4 * mm});
            skSolve(sketch);
        }
        {
            var Q0;
            {var subQ10=sQuery(id+"F1.wireOp",EDGE,"E128");var subQ11=sQuery(id+"F1.wireOp",EDGE,"E133.MirrorCS");var subQ28=sQuery(id+"F1.wireOp",EDGE,"E132.MirrorCS");Q0=makeQuery(id+"FdkW4cJf3UBl0qU_7.boolean.opBoolean","SPLIT",FACE,{"disambiguationData":[TD([makeQuery(id+"F3.opExtrude","SWEPT_FACE",FACE,{"disambiguationData":[OSD([subQ11])]})])],"derivedFrom":makeQuery(id+"F5.opChamfer","BLEND_FACE",FACE,{"disambiguationData":[OSD([subQ10,subQ28])]})});}
            var sketch = newSketch(context, id + "F7", { "sketchPlane" : qUnion([Q0])});
            skLineSegment(sketch, "E159", {"start": v(-153.53, 42.66) * mm, "end": v(-137.59, 19.6) * mm, "construction": true});
            skCircle(sketch, "E160", {"center": v(-145.56, 31.14) * mm, "radius": 6 * mm});
            skCircle(sketch, "E161", {"center": v(-145.56, 31.14) * mm, "radius": 4 * mm});
            skSolve(sketch);
        }
        {
            var Q0;
            {var subQ10=sQuery(id+"F1.wireOp",EDGE,"E128");var subQ12=sQuery(id+"F1.wireOp",EDGE,"E130.right");var subQ28=sQuery(id+"F1.wireOp",EDGE,"E132.MirrorCS");Q0=makeQuery(id+"FdkW4cJf3UBl0qU_7.boolean.opBoolean","SPLIT",FACE,{"disambiguationData":[TD([makeQuery(id+"F3.opExtrude","SWEPT_FACE",FACE,{"disambiguationData":[OSD([subQ12])]})])],"derivedFrom":makeQuery(id+"F5.opChamfer","BLEND_FACE",FACE,{"disambiguationData":[OSD([subQ10,subQ28])]})});}
            var sketch = newSketch(context, id + "F8", { "sketchPlane" : qUnion([Q0])});
            skCircle(sketch, "E162", {"center": v(-205.56, 31.14) * mm, "radius": 6 * mm});
            skCircle(sketch, "E163", {"center": v(-205.56, 31.14) * mm, "radius": 4 * mm});
            skSolve(sketch);
        }
        {
            var Q0;
            Q0=makeQuery(id+"F5.opChamfer","BLEND_FACE",FACE,{"disambiguationData":[OSD([sQuery(id+"F1.wireOp",EDGE,"E140.1.6"),sQuery(id+"F1.wireOp",EDGE,"E140.1.13")])]});
            var sketch = newSketch(context, id + "F9", { "sketchPlane" : qUnion([Q0])});
            skLineSegment(sketch, "E164", {"start": v(-111.36, 49.34) * mm, "end": v(-139.3, 47.1) * mm, "construction": true});
            skLineSegment(sketch, "E165", {"start": v(-139.3, 47.1) * mm, "end": v(-167.16, 81.23) * mm, "construction": true});
            skLineSegment(sketch, "E166", {"start": v(-167.16, 81.23) * mm, "end": v(-159.39, 108.16) * mm, "construction": true});
            skCircle(sketch, "E167", {"center": v(-125.33, 48.22) * mm, "radius": 6 * mm});
            skCircle(sketch, "E168", {"center": v(-163.27, 94.7) * mm, "radius": 6 * mm});
            skCircle(sketch, "E169", {"center": v(-125.33, 48.22) * mm, "radius": 4 * mm});
            skCircle(sketch, "E170", {"center": v(-163.27, 94.7) * mm, "radius": 4 * mm});
            skSolve(sketch);
        }
        {
            var Q0;
            Q0=makeQuery(id+"F5.opChamfer","BLEND_FACE",FACE,{"disambiguationData":[OSD([sQuery(id+"F1.wireOp",EDGE,"E140.2.6"),sQuery(id+"F1.wireOp",EDGE,"E140.2.13")])]});
            var sketch = newSketch(context, id + "F10", { "sketchPlane" : qUnion([Q0])});
            skLineSegment(sketch, "E171", {"start": v(-118.2, 108.16) * mm, "end": v(-110.42, 81.23) * mm, "construction": true});
            skLineSegment(sketch, "E172", {"start": v(-110.42, 81.23) * mm, "end": v(-138.28, 47.1) * mm, "construction": true});
            skLineSegment(sketch, "E173", {"start": v(-138.28, 47.1) * mm, "end": v(-166.22, 49.34) * mm, "construction": true});
            skCircle(sketch, "E174", {"center": v(-152.25, 48.22) * mm, "radius": 6 * mm});
            skCircle(sketch, "E175", {"center": v(-114.3, 94.7) * mm, "radius": 6 * mm});
            skCircle(sketch, "E176", {"center": v(-152.25, 48.22) * mm, "radius": 4 * mm});
            skCircle(sketch, "E177", {"center": v(-114.3, 94.7) * mm, "radius": 4 * mm});
            skSolve(sketch);
        }
        {
            var Q0;
            Q0=makeQuery(id+"F7.imprint","IMPRINT",FACE,{"disambiguationData":[TD([[makeQuery(id+"F7.imprint","IMPRINT",EDGE,{"derivedFrom":sQuery(id+"F7.wireOp",EDGE,"E160")}),1.0]])]});
            var Q1;
            Q1=makeQuery(id+"F8.imprint","IMPRINT",FACE,{"disambiguationData":[TD([[makeQuery(id+"F8.imprint","IMPRINT",EDGE,{"derivedFrom":sQuery(id+"F8.wireOp",EDGE,"E162")}),1.0]])]});
            var Q2;
            Q2=makeQuery(id+"F6.imprint","IMPRINT",FACE,{"disambiguationData":[TD([[makeQuery(id+"F6.imprint","IMPRINT",EDGE,{"derivedFrom":sQuery(id+"F6.wireOp",EDGE,"E155")}),1.0]])]});
            var Q3;
            Q3=makeQuery(id+"F6.imprint","IMPRINT",FACE,{"disambiguationData":[TD([[makeQuery(id+"F6.imprint","IMPRINT",EDGE,{"derivedFrom":sQuery(id+"F6.wireOp",EDGE,"E156")}),1.0]])]});
            extrude(context, id + "F11", {"entities" : qUnion([Q0, Q1, Q2, Q3]), "operationType" : NewBodyOperationType.REMOVE, "oppositeDirection" : true, "depth" : 4 * mm});
        }
        {
            var Q0;
            {var subQ0=sQuery(id+"F0.wireOp",EDGE,"E11");Q0=makeQuery(id+"F5.opChamfer","BLEND_EDGE",EDGE,{"disambiguationData":[OD(0.0)],"blendedFrom":[makeQuery(id+"F3.opExtrude","CAP_EDGE",EDGE,{"disambiguationData":[OSD([sQuery(id+"F0.wireOp",EDGE,"E10"),sQuery(id+"F0.wireOp",EDGE,"E117.bottom")])],"isStart":false}),makeQuery(id+"F3.boolean.opBoolean","MERGE",FACE,{"derivedFrom":[makeQuery(id+"F2.opExtrude","SWEPT_FACE",FACE,{"disambiguationData":[OSD([subQ0])]}),makeQuery(id+"F3.opExtrude","SWEPT_FACE",FACE,{"disambiguationData":[OSD([subQ0,sQuery(id+"F0.wireOp",EDGE,"E121.MirrorCS")])]}),makeQuery(id+"F3.opExtrude","SWEPT_FACE",FACE,{"disambiguationData":[OSD([subQ0,sQuery(id+"F0.wireOp",EDGE,"E117.top")])]})]})],"blendedInto":[makeQuery(id+"F3.boolean.opBoolean","MERGE",FACE,{"derivedFrom":[makeQuery(id+"F2.opExtrude","SWEPT_FACE",FACE,{"disambiguationData":[OSD([subQ0])]}),makeQuery(id+"F3.opExtrude","SWEPT_FACE",FACE,{"disambiguationData":[OSD([subQ0,sQuery(id+"F0.wireOp",EDGE,"E121.MirrorCS")])]}),makeQuery(id+"F3.opExtrude","SWEPT_FACE",FACE,{"disambiguationData":[OSD([subQ0,sQuery(id+"F0.wireOp",EDGE,"E117.top")])]})]})]});}
            var Q1;
            {var subQ0=sQuery(id+"F0.wireOp",EDGE,"E11");Q1=makeQuery(id+"F5.opChamfer","BLEND_EDGE",EDGE,{"disambiguationData":[OD(1.0)],"blendedFrom":[makeQuery(id+"F3.opExtrude","CAP_EDGE",EDGE,{"disambiguationData":[OSD([sQuery(id+"F0.wireOp",EDGE,"E10"),sQuery(id+"F0.wireOp",EDGE,"E117.bottom")])],"isStart":false}),makeQuery(id+"F3.boolean.opBoolean","MERGE",FACE,{"derivedFrom":[makeQuery(id+"F2.opExtrude","SWEPT_FACE",FACE,{"disambiguationData":[OSD([subQ0])]}),makeQuery(id+"F3.opExtrude","SWEPT_FACE",FACE,{"disambiguationData":[OSD([subQ0,sQuery(id+"F0.wireOp",EDGE,"E121.MirrorCS")])]}),makeQuery(id+"F3.opExtrude","SWEPT_FACE",FACE,{"disambiguationData":[OSD([subQ0,sQuery(id+"F0.wireOp",EDGE,"E117.top")])]})]})],"blendedInto":[makeQuery(id+"F3.boolean.opBoolean","MERGE",FACE,{"derivedFrom":[makeQuery(id+"F2.opExtrude","SWEPT_FACE",FACE,{"disambiguationData":[OSD([subQ0])]}),makeQuery(id+"F3.opExtrude","SWEPT_FACE",FACE,{"disambiguationData":[OSD([subQ0,sQuery(id+"F0.wireOp",EDGE,"E121.MirrorCS")])]}),makeQuery(id+"F3.opExtrude","SWEPT_FACE",FACE,{"disambiguationData":[OSD([subQ0,sQuery(id+"F0.wireOp",EDGE,"E117.top")])]})]})]});}
            var Q2;
            Q2=makeQuery(id+"F5.opChamfer","BLEND_EDGE",EDGE,{"blendedFrom":[makeQuery(id+"F3.opExtrude","CAP_EDGE",EDGE,{"disambiguationData":[OSD([sQuery(id+"F0.wireOp",EDGE,"E10"),sQuery(id+"F0.wireOp",EDGE,"E117.bottom")])],"isStart":false}),makeQuery(id+"F3.opExtrude","SWEPT_FACE",FACE,{"disambiguationData":[OSD([sQuery(id+"F0.wireOp",EDGE,"E120.MirrorCS")])]})],"blendedInto":[makeQuery(id+"F3.opExtrude","SWEPT_FACE",FACE,{"disambiguationData":[OSD([sQuery(id+"F0.wireOp",EDGE,"E120.MirrorCS")])]})]});
            var Q3;
            Q3=makeQuery(id+"F5.opChamfer","BLEND_EDGE",EDGE,{"blendedFrom":[makeQuery(id+"F3.opExtrude","CAP_EDGE",EDGE,{"disambiguationData":[OSD([sQuery(id+"F0.wireOp",EDGE,"E10"),sQuery(id+"F0.wireOp",EDGE,"E117.bottom")])],"isStart":false}),makeQuery(id+"F3.opExtrude","SWEPT_FACE",FACE,{"disambiguationData":[OSD([sQuery(id+"F0.wireOp",EDGE,"E125.MirrorCS")])]})],"blendedInto":[makeQuery(id+"F3.opExtrude","SWEPT_FACE",FACE,{"disambiguationData":[OSD([sQuery(id+"F0.wireOp",EDGE,"E125.MirrorCS")])]})]});
            var Q4;
            Q4=makeQuery(id+"F5.opChamfer","BLEND_EDGE",EDGE,{"blendedFrom":[makeQuery(id+"F3.opExtrude","CAP_EDGE",EDGE,{"disambiguationData":[OSD([sQuery(id+"F0.wireOp",EDGE,"E10"),sQuery(id+"F0.wireOp",EDGE,"E117.bottom")])],"isStart":false}),makeQuery(id+"F3.opExtrude","SWEPT_FACE",FACE,{"disambiguationData":[OSD([sQuery(id+"F0.wireOp",EDGE,"E123.MirrorCS")])]})],"blendedInto":[makeQuery(id+"F3.opExtrude","SWEPT_FACE",FACE,{"disambiguationData":[OSD([sQuery(id+"F0.wireOp",EDGE,"E123.MirrorCS")])]})]});
            var Q5;
            Q5=makeQuery(id+"F2.opExtrude","CAP_EDGE",EDGE,{"disambiguationData":[OSD([sQuery(id+"F0.wireOp",EDGE,"E123.MirrorCS")])],"isStart":false});
            var Q6;
            Q6=makeQuery(id+"F3.opExtrude","SWEPT_EDGE",EDGE,{"disambiguationData":[OSD([sQuery(id+"F0.wireOp",EDGE,"E11"),sQuery(id+"F0.wireOp",EDGE,"E123.MirrorCS")])]});
            var Q7;
            Q7=makeQuery(id+"F3.opExtrude","SWEPT_EDGE",EDGE,{"disambiguationData":[OSD([sQuery(id+"F0.wireOp",EDGE,"E11"),sQuery(id+"F0.wireOp",EDGE,"E125.MirrorCS")])]});
            var Q8;
            Q8=makeQuery(id+"F5.opChamfer","BLEND_EDGE",EDGE,{"blendedFrom":[makeQuery(id+"F3.opExtrude","CAP_EDGE",EDGE,{"disambiguationData":[OSD([sQuery(id+"F0.wireOp",EDGE,"E10"),sQuery(id+"F0.wireOp",EDGE,"E117.bottom")])],"isStart":false}),makeQuery(id+"F3.opExtrude","SWEPT_FACE",FACE,{"disambiguationData":[OSD([sQuery(id+"F0.wireOp",EDGE,"E117.right")])]})],"blendedInto":[makeQuery(id+"F3.opExtrude","SWEPT_FACE",FACE,{"disambiguationData":[OSD([sQuery(id+"F0.wireOp",EDGE,"E117.right")])]})]});
            var Q9;
            Q9=makeQuery(id+"F2.opExtrude","CAP_EDGE",EDGE,{"disambiguationData":[OSD([sQuery(id+"F0.wireOp",EDGE,"E125.MirrorCS")])],"isStart":false});
            var Q10;
            {var subQ0=sQuery(id+"F0.wireOp",EDGE,"E117.right");var subQ1=sQuery(id+"F0.wireOp",EDGE,"E117.bottom");Q10=makeQuery(id+"F4.boolean.opBoolean","MERGE",EDGE,{"derivedFrom":[makeQuery(id+"F3.opExtrude","SWEPT_EDGE",EDGE,{"disambiguationData":[OSD([subQ1,subQ0])]}),makeQuery(id+"F4.opExtrude","SWEPT_EDGE",EDGE,{"disambiguationData":[OSD([subQ1,subQ0])]})]});}
            var Q11;
            Q11=makeQuery(id+"F4.opExtrude","CAP_EDGE",EDGE,{"disambiguationData":[OSD([sQuery(id+"F0.wireOp",EDGE,"E10"),sQuery(id+"F0.wireOp",EDGE,"E119.MirrorCS")])],"isStart":false});
            var Q12;
            Q12=makeQuery(id+"F4.opExtrude","CAP_EDGE",EDGE,{"disambiguationData":[OSD([sQuery(id+"F0.wireOp",EDGE,"E120.MirrorCS")])],"isStart":false});
            var Q13;
            Q13=makeQuery(id+"F4.opExtrude","CAP_EDGE",EDGE,{"disambiguationData":[OSD([sQuery(id+"F0.wireOp",EDGE,"E117.right")])],"isStart":false});
            var Q14;
            Q14=makeQuery(id+"F4.opExtrude","CAP_EDGE",EDGE,{"disambiguationData":[OSD([sQuery(id+"F0.wireOp",EDGE,"E10"),sQuery(id+"F0.wireOp",EDGE,"E117.bottom")])],"isStart":false});
            fillet(context, id + "F12", {"entities" : qUnion([Q0, Q1, Q2, Q3, Q4, Q5, Q6, Q7, Q8, Q9, Q10, Q11, Q12, Q13, Q14]), "radius" : 1.5 * mm, "tangentPropagation" : true, "allowEdgeOverflow" : false});
        }
        {
            var Q0;
            Q0=makeQuery(id+"F5.opChamfer","BLEND_EDGE",EDGE,{"blendedFrom":[makeQuery(id+"F3.opExtrude","CAP_EDGE",EDGE,{"disambiguationData":[OSD([sQuery(id+"F1.wireOp",EDGE,"E140.2.6"),sQuery(id+"F1.wireOp",EDGE,"E140.2.13")])],"isStart":false}),makeQuery(id+"F3.opExtrude","SWEPT_FACE",FACE,{"disambiguationData":[OSD([sQuery(id+"F1.wireOp",EDGE,"E140.2.9"),sQuery(id+"F1.wireOp",EDGE,"E140.2.15")])]})],"blendedInto":[makeQuery(id+"F3.opExtrude","SWEPT_FACE",FACE,{"disambiguationData":[OSD([sQuery(id+"F1.wireOp",EDGE,"E140.2.9"),sQuery(id+"F1.wireOp",EDGE,"E140.2.15")])]})]});
            var Q1;
            Q1=makeQuery(id+"F5.opChamfer","BLEND_EDGE",EDGE,{"blendedFrom":[makeQuery(id+"F3.opExtrude","CAP_EDGE",EDGE,{"disambiguationData":[OSD([sQuery(id+"F1.wireOp",EDGE,"E128"),sQuery(id+"F1.wireOp",EDGE,"E132.MirrorCS")])],"isStart":false}),makeQuery(id+"F3.opExtrude","SWEPT_FACE",FACE,{"disambiguationData":[OSD([sQuery(id+"F1.wireOp",EDGE,"E129"),sQuery(id+"F1.wireOp",EDGE,"E130.top")])]})],"blendedInto":[makeQuery(id+"F3.opExtrude","SWEPT_FACE",FACE,{"disambiguationData":[OSD([sQuery(id+"F1.wireOp",EDGE,"E129"),sQuery(id+"F1.wireOp",EDGE,"E130.top")])]})]});
            var Q2;
            Q2=makeQuery(id+"F5.opChamfer","BLEND_EDGE",EDGE,{"blendedFrom":[makeQuery(id+"F3.opExtrude","CAP_EDGE",EDGE,{"disambiguationData":[OSD([sQuery(id+"F1.wireOp",EDGE,"E128"),sQuery(id+"F1.wireOp",EDGE,"E132.MirrorCS")])],"isStart":false}),makeQuery(id+"F3.opExtrude","SWEPT_FACE",FACE,{"disambiguationData":[OSD([sQuery(id+"F1.wireOp",EDGE,"E129"),sQuery(id+"F1.wireOp",EDGE,"E134.MirrorCS")])]})],"blendedInto":[makeQuery(id+"F3.opExtrude","SWEPT_FACE",FACE,{"disambiguationData":[OSD([sQuery(id+"F1.wireOp",EDGE,"E129"),sQuery(id+"F1.wireOp",EDGE,"E134.MirrorCS")])]})]});
            var Q3;
            Q3=makeQuery(id+"F5.opChamfer","BLEND_EDGE",EDGE,{"blendedFrom":[makeQuery(id+"F3.opExtrude","CAP_EDGE",EDGE,{"disambiguationData":[OSD([sQuery(id+"F1.wireOp",EDGE,"E140.1.6"),sQuery(id+"F1.wireOp",EDGE,"E140.1.13")])],"isStart":false}),makeQuery(id+"F3.opExtrude","SWEPT_FACE",FACE,{"disambiguationData":[OSD([sQuery(id+"F1.wireOp",EDGE,"E140.1.9"),sQuery(id+"F1.wireOp",EDGE,"E140.1.12")])]})],"blendedInto":[makeQuery(id+"F3.opExtrude","SWEPT_FACE",FACE,{"disambiguationData":[OSD([sQuery(id+"F1.wireOp",EDGE,"E140.1.9"),sQuery(id+"F1.wireOp",EDGE,"E140.1.12")])]})]});
            var Q4;
            Q4=makeQuery(id+"F5.opChamfer","BLEND_EDGE",EDGE,{"blendedFrom":[makeQuery(id+"F3.opExtrude","CAP_EDGE",EDGE,{"disambiguationData":[OSD([sQuery(id+"F1.wireOp",EDGE,"E140.1.6"),sQuery(id+"F1.wireOp",EDGE,"E140.1.13")])],"isStart":false}),makeQuery(id+"F3.opExtrude","SWEPT_FACE",FACE,{"disambiguationData":[OSD([sQuery(id+"F1.wireOp",EDGE,"E140.1.9"),sQuery(id+"F1.wireOp",EDGE,"E140.1.15")])]})],"blendedInto":[makeQuery(id+"F3.opExtrude","SWEPT_FACE",FACE,{"disambiguationData":[OSD([sQuery(id+"F1.wireOp",EDGE,"E140.1.9"),sQuery(id+"F1.wireOp",EDGE,"E140.1.15")])]})]});
            var Q5;
            Q5=makeQuery(id+"F5.opChamfer","BLEND_EDGE",EDGE,{"blendedFrom":[makeQuery(id+"F3.opExtrude","CAP_EDGE",EDGE,{"disambiguationData":[OSD([sQuery(id+"F1.wireOp",EDGE,"E140.2.6"),sQuery(id+"F1.wireOp",EDGE,"E140.2.13")])],"isStart":false}),makeQuery(id+"F3.opExtrude","SWEPT_FACE",FACE,{"disambiguationData":[OSD([sQuery(id+"F1.wireOp",EDGE,"E140.2.9"),sQuery(id+"F1.wireOp",EDGE,"E140.2.12")])]})],"blendedInto":[makeQuery(id+"F3.opExtrude","SWEPT_FACE",FACE,{"disambiguationData":[OSD([sQuery(id+"F1.wireOp",EDGE,"E140.2.9"),sQuery(id+"F1.wireOp",EDGE,"E140.2.12")])]})]});
            var Q6;
            Q6=makeQuery(id+"F5.opChamfer","BLEND_EDGE",EDGE,{"blendedFrom":[makeQuery(id+"F3.opExtrude","CAP_EDGE",EDGE,{"disambiguationData":[OSD([sQuery(id+"F1.wireOp",EDGE,"E128"),sQuery(id+"F1.wireOp",EDGE,"E132.MirrorCS")])],"isStart":false}),makeQuery(id+"F3.opExtrude","SWEPT_FACE",FACE,{"disambiguationData":[OSD([sQuery(id+"F1.wireOp",EDGE,"E133.MirrorCS")])]})],"blendedInto":[makeQuery(id+"F3.opExtrude","SWEPT_FACE",FACE,{"disambiguationData":[OSD([sQuery(id+"F1.wireOp",EDGE,"E133.MirrorCS")])]})]});
            var Q7;
            Q7=makeQuery(id+"F5.opChamfer","BLEND_EDGE",EDGE,{"blendedFrom":[makeQuery(id+"F3.opExtrude","CAP_EDGE",EDGE,{"disambiguationData":[OSD([sQuery(id+"F1.wireOp",EDGE,"E128"),sQuery(id+"F1.wireOp",EDGE,"E132.MirrorCS")])],"isStart":false}),makeQuery(id+"F3.opExtrude","SWEPT_FACE",FACE,{"disambiguationData":[OSD([sQuery(id+"F1.wireOp",EDGE,"E130.right")])]})],"blendedInto":[makeQuery(id+"F3.opExtrude","SWEPT_FACE",FACE,{"disambiguationData":[OSD([sQuery(id+"F1.wireOp",EDGE,"E130.right")])]})]});
            var Q8;
            Q8=makeQuery(id+"F5.opChamfer","BLEND_EDGE",EDGE,{"blendedFrom":[makeQuery(id+"F3.opExtrude","CAP_EDGE",EDGE,{"disambiguationData":[OSD([sQuery(id+"F1.wireOp",EDGE,"E140.1.6"),sQuery(id+"F1.wireOp",EDGE,"E140.1.13")])],"isStart":false}),makeQuery(id+"F3.opExtrude","SWEPT_FACE",FACE,{"disambiguationData":[OSD([sQuery(id+"F1.wireOp",EDGE,"E140.1.0")])]})],"blendedInto":[makeQuery(id+"F3.opExtrude","SWEPT_FACE",FACE,{"disambiguationData":[OSD([sQuery(id+"F1.wireOp",EDGE,"E140.1.0")])]})]});
            var Q9;
            Q9=makeQuery(id+"F5.opChamfer","BLEND_EDGE",EDGE,{"blendedFrom":[makeQuery(id+"F3.opExtrude","CAP_EDGE",EDGE,{"disambiguationData":[OSD([sQuery(id+"F1.wireOp",EDGE,"E140.1.6"),sQuery(id+"F1.wireOp",EDGE,"E140.1.13")])],"isStart":false}),makeQuery(id+"F3.opExtrude","SWEPT_FACE",FACE,{"disambiguationData":[OSD([sQuery(id+"F1.wireOp",EDGE,"E140.1.5")])]})],"blendedInto":[makeQuery(id+"F3.opExtrude","SWEPT_FACE",FACE,{"disambiguationData":[OSD([sQuery(id+"F1.wireOp",EDGE,"E140.1.5")])]})]});
            var Q10;
            Q10=makeQuery(id+"F5.opChamfer","BLEND_EDGE",EDGE,{"blendedFrom":[makeQuery(id+"F3.opExtrude","CAP_EDGE",EDGE,{"disambiguationData":[OSD([sQuery(id+"F1.wireOp",EDGE,"E140.2.6"),sQuery(id+"F1.wireOp",EDGE,"E140.2.13")])],"isStart":false}),makeQuery(id+"F3.opExtrude","SWEPT_FACE",FACE,{"disambiguationData":[OSD([sQuery(id+"F1.wireOp",EDGE,"E140.2.5")])]})],"blendedInto":[makeQuery(id+"F3.opExtrude","SWEPT_FACE",FACE,{"disambiguationData":[OSD([sQuery(id+"F1.wireOp",EDGE,"E140.2.5")])]})]});
            var Q11;
            Q11=makeQuery(id+"F5.opChamfer","BLEND_EDGE",EDGE,{"blendedFrom":[makeQuery(id+"F3.opExtrude","CAP_EDGE",EDGE,{"disambiguationData":[OSD([sQuery(id+"F1.wireOp",EDGE,"E140.2.6"),sQuery(id+"F1.wireOp",EDGE,"E140.2.13")])],"isStart":false}),makeQuery(id+"F3.opExtrude","SWEPT_FACE",FACE,{"disambiguationData":[OSD([sQuery(id+"F1.wireOp",EDGE,"E140.2.0")])]})],"blendedInto":[makeQuery(id+"F3.opExtrude","SWEPT_FACE",FACE,{"disambiguationData":[OSD([sQuery(id+"F1.wireOp",EDGE,"E140.2.0")])]})]});
            var Q12;
            Q12=makeQuery(id+"F5.opChamfer","BLEND_EDGE",EDGE,{"blendedFrom":[makeQuery(id+"F3.opExtrude","CAP_EDGE",EDGE,{"disambiguationData":[OSD([sQuery(id+"F1.wireOp",EDGE,"E140.2.6"),sQuery(id+"F1.wireOp",EDGE,"E140.2.13")])],"isStart":false}),makeQuery(id+"F3.opExtrude","SWEPT_FACE",FACE,{"disambiguationData":[OSD([sQuery(id+"F1.wireOp",EDGE,"E140.2.1")])]})],"blendedInto":[makeQuery(id+"F3.opExtrude","SWEPT_FACE",FACE,{"disambiguationData":[OSD([sQuery(id+"F1.wireOp",EDGE,"E140.2.1")])]})]});
            var Q13;
            {var subQ0=sQuery(id+"F1.wireOp",EDGE,"E140.2.6");Q13=makeQuery(id+"F5.opChamfer","BLEND_EDGE",EDGE,{"blendedFrom":[makeQuery(id+"F3.opExtrude","CAP_EDGE",EDGE,{"disambiguationData":[OSD([subQ0,sQuery(id+"F1.wireOp",EDGE,"E140.2.13")])],"isStart":false}),makeQuery(id+"F2.opExtrude","CAP_FACE",FACE,{"disambiguationData":[OSD([sQuery(id+"F1.wireOp",EDGE,"E128"),sQuery(id+"F1.wireOp",EDGE,"E129"),sQuery(id+"F1.wireOp",EDGE,"f1ae98ec-eddd-4e72-9429-8ecdf1ed458a"),sQuery(id+"F1.wireOp",EDGE,"4aa6aff6-2e9c-42ca-a4fd-632af8ab0357"),sQuery(id+"F1.wireOp",EDGE,"E130.top"),sQuery(id+"F1.wireOp",EDGE,"E134.MirrorCS"),sQuery(id+"F1.wireOp",EDGE,"E136.MirrorCS"),sQuery(id+"F1.wireOp",EDGE,"E138.MirrorCS"),sQuery(id+"F1.wireOp",EDGE,"E140.1.1"),sQuery(id+"F1.wireOp",EDGE,"E140.1.2"),sQuery(id+"F1.wireOp",EDGE,"E140.1.6"),sQuery(id+"F1.wireOp",EDGE,"E140.1.9"),sQuery(id+"F1.wireOp",EDGE,"E140.1.10"),sQuery(id+"F1.wireOp",EDGE,"E140.1.11"),sQuery(id+"F1.wireOp",EDGE,"E140.1.12"),sQuery(id+"F1.wireOp",EDGE,"E140.1.15"),sQuery(id+"F1.wireOp",EDGE,"E140.2.1"),sQuery(id+"F1.wireOp",EDGE,"E140.2.2"),subQ0,sQuery(id+"F1.wireOp",EDGE,"E140.2.9"),sQuery(id+"F1.wireOp",EDGE,"E140.2.10"),sQuery(id+"F1.wireOp",EDGE,"E140.2.11"),sQuery(id+"F1.wireOp",EDGE,"E140.2.12"),sQuery(id+"F1.wireOp",EDGE,"E140.2.15"),sQuery(id+"F1.wireOp",EDGE,"E141"),sQuery(id+"F1.wireOp",EDGE,"E142"),sQuery(id+"F1.wireOp",EDGE,"E143")])],"isStart":false})],"blendedInto":[makeQuery(id+"F2.opExtrude","CAP_FACE",FACE,{"disambiguationData":[OSD([sQuery(id+"F1.wireOp",EDGE,"E128"),sQuery(id+"F1.wireOp",EDGE,"E129"),sQuery(id+"F1.wireOp",EDGE,"f1ae98ec-eddd-4e72-9429-8ecdf1ed458a"),sQuery(id+"F1.wireOp",EDGE,"4aa6aff6-2e9c-42ca-a4fd-632af8ab0357"),sQuery(id+"F1.wireOp",EDGE,"E130.top"),sQuery(id+"F1.wireOp",EDGE,"E134.MirrorCS"),sQuery(id+"F1.wireOp",EDGE,"E136.MirrorCS"),sQuery(id+"F1.wireOp",EDGE,"E138.MirrorCS"),sQuery(id+"F1.wireOp",EDGE,"E140.1.1"),sQuery(id+"F1.wireOp",EDGE,"E140.1.2"),sQuery(id+"F1.wireOp",EDGE,"E140.1.6"),sQuery(id+"F1.wireOp",EDGE,"E140.1.9"),sQuery(id+"F1.wireOp",EDGE,"E140.1.10"),sQuery(id+"F1.wireOp",EDGE,"E140.1.11"),sQuery(id+"F1.wireOp",EDGE,"E140.1.12"),sQuery(id+"F1.wireOp",EDGE,"E140.1.15"),sQuery(id+"F1.wireOp",EDGE,"E140.2.1"),sQuery(id+"F1.wireOp",EDGE,"E140.2.2"),subQ0,sQuery(id+"F1.wireOp",EDGE,"E140.2.9"),sQuery(id+"F1.wireOp",EDGE,"E140.2.10"),sQuery(id+"F1.wireOp",EDGE,"E140.2.11"),sQuery(id+"F1.wireOp",EDGE,"E140.2.12"),sQuery(id+"F1.wireOp",EDGE,"E140.2.15"),sQuery(id+"F1.wireOp",EDGE,"E141"),sQuery(id+"F1.wireOp",EDGE,"E142"),sQuery(id+"F1.wireOp",EDGE,"E143")])],"isStart":false})]});}
            var Q14;
            Q14=makeQuery(id+"F5.opChamfer","BLEND_EDGE",EDGE,{"blendedFrom":[makeQuery(id+"F3.opExtrude","CAP_EDGE",EDGE,{"disambiguationData":[OSD([sQuery(id+"F1.wireOp",EDGE,"E140.2.6"),sQuery(id+"F1.wireOp",EDGE,"E140.2.13")])],"isStart":false}),makeQuery(id+"F3.opExtrude","SWEPT_FACE",FACE,{"disambiguationData":[OSD([sQuery(id+"F1.wireOp",EDGE,"E140.2.2")])]})],"blendedInto":[makeQuery(id+"F3.opExtrude","SWEPT_FACE",FACE,{"disambiguationData":[OSD([sQuery(id+"F1.wireOp",EDGE,"E140.2.2")])]})]});
            var Q15;
            Q15=makeQuery(id+"F5.opChamfer","BLEND_EDGE",EDGE,{"blendedFrom":[makeQuery(id+"F3.opExtrude","CAP_EDGE",EDGE,{"disambiguationData":[OSD([sQuery(id+"F1.wireOp",EDGE,"E140.1.6"),sQuery(id+"F1.wireOp",EDGE,"E140.1.13")])],"isStart":false}),makeQuery(id+"F3.opExtrude","SWEPT_FACE",FACE,{"disambiguationData":[OSD([sQuery(id+"F1.wireOp",EDGE,"E140.1.2")])]})],"blendedInto":[makeQuery(id+"F3.opExtrude","SWEPT_FACE",FACE,{"disambiguationData":[OSD([sQuery(id+"F1.wireOp",EDGE,"E140.1.2")])]})]});
            var Q16;
            {var subQ0=sQuery(id+"F1.wireOp",EDGE,"E140.1.6");Q16=makeQuery(id+"F5.opChamfer","BLEND_EDGE",EDGE,{"blendedFrom":[makeQuery(id+"F3.opExtrude","CAP_EDGE",EDGE,{"disambiguationData":[OSD([subQ0,sQuery(id+"F1.wireOp",EDGE,"E140.1.13")])],"isStart":false}),makeQuery(id+"F2.opExtrude","CAP_FACE",FACE,{"disambiguationData":[OSD([sQuery(id+"F1.wireOp",EDGE,"E128"),sQuery(id+"F1.wireOp",EDGE,"E129"),sQuery(id+"F1.wireOp",EDGE,"f1ae98ec-eddd-4e72-9429-8ecdf1ed458a"),sQuery(id+"F1.wireOp",EDGE,"4aa6aff6-2e9c-42ca-a4fd-632af8ab0357"),sQuery(id+"F1.wireOp",EDGE,"E130.top"),sQuery(id+"F1.wireOp",EDGE,"E134.MirrorCS"),sQuery(id+"F1.wireOp",EDGE,"E136.MirrorCS"),sQuery(id+"F1.wireOp",EDGE,"E138.MirrorCS"),sQuery(id+"F1.wireOp",EDGE,"E140.1.1"),sQuery(id+"F1.wireOp",EDGE,"E140.1.2"),subQ0,sQuery(id+"F1.wireOp",EDGE,"E140.1.9"),sQuery(id+"F1.wireOp",EDGE,"E140.1.10"),sQuery(id+"F1.wireOp",EDGE,"E140.1.11"),sQuery(id+"F1.wireOp",EDGE,"E140.1.12"),sQuery(id+"F1.wireOp",EDGE,"E140.1.15"),sQuery(id+"F1.wireOp",EDGE,"E140.2.1"),sQuery(id+"F1.wireOp",EDGE,"E140.2.2"),sQuery(id+"F1.wireOp",EDGE,"E140.2.6"),sQuery(id+"F1.wireOp",EDGE,"E140.2.9"),sQuery(id+"F1.wireOp",EDGE,"E140.2.10"),sQuery(id+"F1.wireOp",EDGE,"E140.2.11"),sQuery(id+"F1.wireOp",EDGE,"E140.2.12"),sQuery(id+"F1.wireOp",EDGE,"E140.2.15"),sQuery(id+"F1.wireOp",EDGE,"E141"),sQuery(id+"F1.wireOp",EDGE,"E142"),sQuery(id+"F1.wireOp",EDGE,"E143")])],"isStart":false})],"blendedInto":[makeQuery(id+"F2.opExtrude","CAP_FACE",FACE,{"disambiguationData":[OSD([sQuery(id+"F1.wireOp",EDGE,"E128"),sQuery(id+"F1.wireOp",EDGE,"E129"),sQuery(id+"F1.wireOp",EDGE,"f1ae98ec-eddd-4e72-9429-8ecdf1ed458a"),sQuery(id+"F1.wireOp",EDGE,"4aa6aff6-2e9c-42ca-a4fd-632af8ab0357"),sQuery(id+"F1.wireOp",EDGE,"E130.top"),sQuery(id+"F1.wireOp",EDGE,"E134.MirrorCS"),sQuery(id+"F1.wireOp",EDGE,"E136.MirrorCS"),sQuery(id+"F1.wireOp",EDGE,"E138.MirrorCS"),sQuery(id+"F1.wireOp",EDGE,"E140.1.1"),sQuery(id+"F1.wireOp",EDGE,"E140.1.2"),subQ0,sQuery(id+"F1.wireOp",EDGE,"E140.1.9"),sQuery(id+"F1.wireOp",EDGE,"E140.1.10"),sQuery(id+"F1.wireOp",EDGE,"E140.1.11"),sQuery(id+"F1.wireOp",EDGE,"E140.1.12"),sQuery(id+"F1.wireOp",EDGE,"E140.1.15"),sQuery(id+"F1.wireOp",EDGE,"E140.2.1"),sQuery(id+"F1.wireOp",EDGE,"E140.2.2"),sQuery(id+"F1.wireOp",EDGE,"E140.2.6"),sQuery(id+"F1.wireOp",EDGE,"E140.2.9"),sQuery(id+"F1.wireOp",EDGE,"E140.2.10"),sQuery(id+"F1.wireOp",EDGE,"E140.2.11"),sQuery(id+"F1.wireOp",EDGE,"E140.2.12"),sQuery(id+"F1.wireOp",EDGE,"E140.2.15"),sQuery(id+"F1.wireOp",EDGE,"E141"),sQuery(id+"F1.wireOp",EDGE,"E142"),sQuery(id+"F1.wireOp",EDGE,"E143")])],"isStart":false})]});}
            var Q17;
            Q17=makeQuery(id+"F5.opChamfer","BLEND_EDGE",EDGE,{"blendedFrom":[makeQuery(id+"F3.opExtrude","CAP_EDGE",EDGE,{"disambiguationData":[OSD([sQuery(id+"F1.wireOp",EDGE,"E140.1.6"),sQuery(id+"F1.wireOp",EDGE,"E140.1.13")])],"isStart":false}),makeQuery(id+"F3.opExtrude","SWEPT_FACE",FACE,{"disambiguationData":[OSD([sQuery(id+"F1.wireOp",EDGE,"E140.1.1")])]})],"blendedInto":[makeQuery(id+"F3.opExtrude","SWEPT_FACE",FACE,{"disambiguationData":[OSD([sQuery(id+"F1.wireOp",EDGE,"E140.1.1")])]})]});
            var Q18;
            Q18=makeQuery(id+"F5.opChamfer","BLEND_EDGE",EDGE,{"blendedFrom":[makeQuery(id+"F3.opExtrude","CAP_EDGE",EDGE,{"disambiguationData":[OSD([sQuery(id+"F1.wireOp",EDGE,"E128"),sQuery(id+"F1.wireOp",EDGE,"E132.MirrorCS")])],"isStart":false}),makeQuery(id+"F3.opExtrude","SWEPT_FACE",FACE,{"disambiguationData":[OSD([sQuery(id+"F1.wireOp",EDGE,"E138.MirrorCS")])]})],"blendedInto":[makeQuery(id+"F3.opExtrude","SWEPT_FACE",FACE,{"disambiguationData":[OSD([sQuery(id+"F1.wireOp",EDGE,"E138.MirrorCS")])]})]});
            var Q19;
            {var subQ0=sQuery(id+"F1.wireOp",EDGE,"E128");Q19=makeQuery(id+"F5.opChamfer","BLEND_EDGE",EDGE,{"blendedFrom":[makeQuery(id+"F3.opExtrude","CAP_EDGE",EDGE,{"disambiguationData":[OSD([subQ0,sQuery(id+"F1.wireOp",EDGE,"E132.MirrorCS")])],"isStart":false}),makeQuery(id+"F2.opExtrude","CAP_FACE",FACE,{"disambiguationData":[OSD([subQ0,sQuery(id+"F1.wireOp",EDGE,"E129"),sQuery(id+"F1.wireOp",EDGE,"f1ae98ec-eddd-4e72-9429-8ecdf1ed458a"),sQuery(id+"F1.wireOp",EDGE,"4aa6aff6-2e9c-42ca-a4fd-632af8ab0357"),sQuery(id+"F1.wireOp",EDGE,"E130.top"),sQuery(id+"F1.wireOp",EDGE,"E134.MirrorCS"),sQuery(id+"F1.wireOp",EDGE,"E136.MirrorCS"),sQuery(id+"F1.wireOp",EDGE,"E138.MirrorCS"),sQuery(id+"F1.wireOp",EDGE,"E140.1.1"),sQuery(id+"F1.wireOp",EDGE,"E140.1.2"),sQuery(id+"F1.wireOp",EDGE,"E140.1.6"),sQuery(id+"F1.wireOp",EDGE,"E140.1.9"),sQuery(id+"F1.wireOp",EDGE,"E140.1.10"),sQuery(id+"F1.wireOp",EDGE,"E140.1.11"),sQuery(id+"F1.wireOp",EDGE,"E140.1.12"),sQuery(id+"F1.wireOp",EDGE,"E140.1.15"),sQuery(id+"F1.wireOp",EDGE,"E140.2.1"),sQuery(id+"F1.wireOp",EDGE,"E140.2.2"),sQuery(id+"F1.wireOp",EDGE,"E140.2.6"),sQuery(id+"F1.wireOp",EDGE,"E140.2.9"),sQuery(id+"F1.wireOp",EDGE,"E140.2.10"),sQuery(id+"F1.wireOp",EDGE,"E140.2.11"),sQuery(id+"F1.wireOp",EDGE,"E140.2.12"),sQuery(id+"F1.wireOp",EDGE,"E140.2.15"),sQuery(id+"F1.wireOp",EDGE,"E141"),sQuery(id+"F1.wireOp",EDGE,"E142"),sQuery(id+"F1.wireOp",EDGE,"E143")])],"isStart":false})],"blendedInto":[makeQuery(id+"F2.opExtrude","CAP_FACE",FACE,{"disambiguationData":[OSD([subQ0,sQuery(id+"F1.wireOp",EDGE,"E129"),sQuery(id+"F1.wireOp",EDGE,"f1ae98ec-eddd-4e72-9429-8ecdf1ed458a"),sQuery(id+"F1.wireOp",EDGE,"4aa6aff6-2e9c-42ca-a4fd-632af8ab0357"),sQuery(id+"F1.wireOp",EDGE,"E130.top"),sQuery(id+"F1.wireOp",EDGE,"E134.MirrorCS"),sQuery(id+"F1.wireOp",EDGE,"E136.MirrorCS"),sQuery(id+"F1.wireOp",EDGE,"E138.MirrorCS"),sQuery(id+"F1.wireOp",EDGE,"E140.1.1"),sQuery(id+"F1.wireOp",EDGE,"E140.1.2"),sQuery(id+"F1.wireOp",EDGE,"E140.1.6"),sQuery(id+"F1.wireOp",EDGE,"E140.1.9"),sQuery(id+"F1.wireOp",EDGE,"E140.1.10"),sQuery(id+"F1.wireOp",EDGE,"E140.1.11"),sQuery(id+"F1.wireOp",EDGE,"E140.1.12"),sQuery(id+"F1.wireOp",EDGE,"E140.1.15"),sQuery(id+"F1.wireOp",EDGE,"E140.2.1"),sQuery(id+"F1.wireOp",EDGE,"E140.2.2"),sQuery(id+"F1.wireOp",EDGE,"E140.2.6"),sQuery(id+"F1.wireOp",EDGE,"E140.2.9"),sQuery(id+"F1.wireOp",EDGE,"E140.2.10"),sQuery(id+"F1.wireOp",EDGE,"E140.2.11"),sQuery(id+"F1.wireOp",EDGE,"E140.2.12"),sQuery(id+"F1.wireOp",EDGE,"E140.2.15"),sQuery(id+"F1.wireOp",EDGE,"E141"),sQuery(id+"F1.wireOp",EDGE,"E142"),sQuery(id+"F1.wireOp",EDGE,"E143")])],"isStart":false})]});}
            var Q20;
            Q20=makeQuery(id+"F5.opChamfer","BLEND_EDGE",EDGE,{"blendedFrom":[makeQuery(id+"F3.opExtrude","CAP_EDGE",EDGE,{"disambiguationData":[OSD([sQuery(id+"F1.wireOp",EDGE,"E128"),sQuery(id+"F1.wireOp",EDGE,"E132.MirrorCS")])],"isStart":false}),makeQuery(id+"F3.opExtrude","SWEPT_FACE",FACE,{"disambiguationData":[OSD([sQuery(id+"F1.wireOp",EDGE,"E136.MirrorCS")])]})],"blendedInto":[makeQuery(id+"F3.opExtrude","SWEPT_FACE",FACE,{"disambiguationData":[OSD([sQuery(id+"F1.wireOp",EDGE,"E136.MirrorCS")])]})]});
            var Q21;
            Q21=makeQuery(id+"F2.opExtrude","CAP_EDGE",EDGE,{"disambiguationData":[OSD([sQuery(id+"F1.wireOp",EDGE,"E140.1.9"),sQuery(id+"F1.wireOp",EDGE,"E140.1.12")])],"isStart":false});
            var Q22;
            Q22=makeQuery(id+"F2.opExtrude","CAP_EDGE",EDGE,{"disambiguationData":[OSD([sQuery(id+"F1.wireOp",EDGE,"E129"),sQuery(id+"F1.wireOp",EDGE,"E134.MirrorCS")])],"isStart":false});
            var Q23;
            Q23=makeQuery(id+"F2.opExtrude","CAP_EDGE",EDGE,{"disambiguationData":[OSD([sQuery(id+"F1.wireOp",EDGE,"E138.MirrorCS")])],"isStart":false});
            var Q24;
            Q24=makeQuery(id+"F2.opExtrude","CAP_EDGE",EDGE,{"disambiguationData":[OSD([sQuery(id+"F1.wireOp",EDGE,"E129"),sQuery(id+"F1.wireOp",EDGE,"E130.top")])],"isStart":false});
            var Q25;
            Q25=makeQuery(id+"F2.opExtrude","CAP_EDGE",EDGE,{"disambiguationData":[OSD([sQuery(id+"F1.wireOp",EDGE,"E136.MirrorCS")])],"isStart":false});
            var Q26;
            Q26=makeQuery(id+"F2.opExtrude","CAP_EDGE",EDGE,{"disambiguationData":[OSD([sQuery(id+"F1.wireOp",EDGE,"E140.2.2")])],"isStart":false});
            var Q27;
            Q27=makeQuery(id+"F2.opExtrude","CAP_EDGE",EDGE,{"disambiguationData":[OSD([sQuery(id+"F1.wireOp",EDGE,"E140.1.9"),sQuery(id+"F1.wireOp",EDGE,"E140.1.15")])],"isStart":false});
            var Q28;
            Q28=makeQuery(id+"F2.opExtrude","CAP_EDGE",EDGE,{"disambiguationData":[OSD([sQuery(id+"F1.wireOp",EDGE,"E140.1.2")])],"isStart":false});
            var Q29;
            Q29=makeQuery(id+"F2.opExtrude","CAP_EDGE",EDGE,{"disambiguationData":[OSD([sQuery(id+"F1.wireOp",EDGE,"E140.2.9"),sQuery(id+"F1.wireOp",EDGE,"E140.2.12")])],"isStart":false});
            var Q30;
            Q30=makeQuery(id+"F2.opExtrude","CAP_EDGE",EDGE,{"disambiguationData":[OSD([sQuery(id+"F1.wireOp",EDGE,"E140.2.1")])],"isStart":false});
            var Q31;
            Q31=makeQuery(id+"F2.opExtrude","CAP_EDGE",EDGE,{"disambiguationData":[OSD([sQuery(id+"F1.wireOp",EDGE,"E140.1.1")])],"isStart":false});
            fillet(context, id + "F13", {"entities" : qUnion([Q0, Q1, Q2, Q3, Q4, Q5, Q6, Q7, Q8, Q9, Q10, Q11, Q12, Q13, Q14, Q15, Q16, Q17, Q18, Q19, Q20, Q21, Q22, Q23, Q24, Q25, Q26, Q27, Q28, Q29, Q30, Q31]), "radius" : 1.5 * mm, "tangentPropagation" : true, "allowEdgeOverflow" : false});
        }
        {
            var Q0;
            Q0=makeQuery(id+"F10.imprint","IMPRINT",FACE,{"disambiguationData":[TD([[makeQuery(id+"F10.imprint","IMPRINT",EDGE,{"derivedFrom":sQuery(id+"F10.wireOp",EDGE,"E174")}),1.0]])]});
            var Q1;
            Q1=makeQuery(id+"F10.imprint","IMPRINT",FACE,{"disambiguationData":[TD([[makeQuery(id+"F10.imprint","IMPRINT",EDGE,{"derivedFrom":sQuery(id+"F10.wireOp",EDGE,"E175")}),1.0]])]});
            extrude(context, id + "F14", {"entities" : qUnion([Q0, Q1]), "operationType" : NewBodyOperationType.REMOVE, "oppositeDirection" : true, "depth" : 4 * mm});
        }
        {
            var Q0;
            Q0=makeQuery(id+"F9.imprint","IMPRINT",FACE,{"disambiguationData":[TD([[makeQuery(id+"F9.imprint","IMPRINT",EDGE,{"derivedFrom":sQuery(id+"F9.wireOp",EDGE,"E168")}),1.0]])]});
            var Q1;
            Q1=makeQuery(id+"F9.imprint","IMPRINT",FACE,{"disambiguationData":[TD([[makeQuery(id+"F9.imprint","IMPRINT",EDGE,{"derivedFrom":sQuery(id+"F9.wireOp",EDGE,"E167")}),1.0]])]});
            extrude(context, id + "F15", {"entities" : qUnion([Q0, Q1]), "operationType" : NewBodyOperationType.REMOVE, "oppositeDirection" : true, "depth" : 4 * mm});
        }
        {
            var Q0;
            Q0=makeQuery(id+"F8.imprint","IMPRINT",FACE,{"disambiguationData":[TD([[makeQuery(id+"F8.imprint","IMPRINT",EDGE,{"derivedFrom":sQuery(id+"F8.wireOp",EDGE,"E163")}),1.0]])]});
            var Q1;
            Q1=makeQuery(id+"F7.imprint","IMPRINT",FACE,{"disambiguationData":[TD([[makeQuery(id+"F7.imprint","IMPRINT",EDGE,{"derivedFrom":sQuery(id+"F7.wireOp",EDGE,"E161")}),1.0]])]});
            var Q2;
            Q2=makeQuery(id+"F11.boolean.opBoolean","SPLIT",FACE,{"disambiguationData":[TD([makeQuery(id+"F11.opExtrude","SWEPT_FACE",FACE,{"disambiguationData":[OSD([sQuery(id+"F6.wireOp",EDGE,"E157")])]})])],"derivedFrom":makeQuery(id+"F5.opChamfer","BLEND_FACE",FACE,{"disambiguationData":[OSD([sQuery(id+"F0.wireOp",EDGE,"E10"),sQuery(id+"F0.wireOp",EDGE,"E117.bottom")])]})});
            var Q3;
            Q3=makeQuery(id+"F11.boolean.opBoolean","SPLIT",FACE,{"disambiguationData":[TD([makeQuery(id+"F11.opExtrude","SWEPT_FACE",FACE,{"disambiguationData":[OSD([sQuery(id+"F6.wireOp",EDGE,"E158")])]})])],"derivedFrom":makeQuery(id+"F5.opChamfer","BLEND_FACE",FACE,{"disambiguationData":[OSD([sQuery(id+"F0.wireOp",EDGE,"E10"),sQuery(id+"F0.wireOp",EDGE,"E117.bottom")])]})});
            extrude(context, id + "F16", {"entities" : qUnion([Q0, Q1, Q2, Q3]), "operationType" : NewBodyOperationType.REMOVE, "oppositeDirection" : true, "depth" : 8 * mm});
        }
        {
            var Q0;
            Q0=makeQuery(id+"F14.boolean.opBoolean","SPLIT",FACE,{"disambiguationData":[TD([makeQuery(id+"F14.opExtrude","SWEPT_FACE",FACE,{"disambiguationData":[OSD([sQuery(id+"F10.wireOp",EDGE,"E177")])]})])],"derivedFrom":makeQuery(id+"F5.opChamfer","BLEND_FACE",FACE,{"disambiguationData":[OSD([sQuery(id+"F1.wireOp",EDGE,"E140.2.6"),sQuery(id+"F1.wireOp",EDGE,"E140.2.13")])]})});
            var Q1;
            Q1=makeQuery(id+"F14.boolean.opBoolean","SPLIT",FACE,{"disambiguationData":[TD([makeQuery(id+"F14.opExtrude","SWEPT_FACE",FACE,{"disambiguationData":[OSD([sQuery(id+"F10.wireOp",EDGE,"E176")])]})])],"derivedFrom":makeQuery(id+"F5.opChamfer","BLEND_FACE",FACE,{"disambiguationData":[OSD([sQuery(id+"F1.wireOp",EDGE,"E140.2.6"),sQuery(id+"F1.wireOp",EDGE,"E140.2.13")])]})});
            extrude(context, id + "F17", {"entities" : qUnion([Q0, Q1]), "operationType" : NewBodyOperationType.REMOVE, "oppositeDirection" : true, "depth" : 8 * mm});
        }
        {
            var Q0;
            Q0=makeQuery(id+"F9.imprint","IMPRINT",FACE,{"disambiguationData":[TD([[makeQuery(id+"F9.imprint","IMPRINT",EDGE,{"derivedFrom":sQuery(id+"F9.wireOp",EDGE,"E170")}),1.0]])]});
            var Q1;
            Q1=makeQuery(id+"F9.imprint","IMPRINT",FACE,{"disambiguationData":[TD([[makeQuery(id+"F9.imprint","IMPRINT",EDGE,{"derivedFrom":sQuery(id+"F9.wireOp",EDGE,"E169")}),1.0]])]});
            extrude(context, id + "F18", {"entities" : qUnion([Q0, Q1]), "operationType" : NewBodyOperationType.REMOVE, "oppositeDirection" : true, "depth" : 8 * mm});
        }
        {
            var Q0;
            Q0=qCreatedBy(makeId("Top.planeOp"),FACE);
            var sketch = newSketch(context, id + "F19", { "sketchPlane" : qUnion([Q0])});
            skCircle(sketch, "E178", {"center": v(-81.36, -54.16) * mm, "radius": 3.5 * mm});
            skCircle(sketch, "E179", {"center": v(-81.36, -54.16) * mm, "radius": 1.6 * mm});
            skSolve(sketch);
        }
        {
            var Q0;
            Q0=makeQuery(id+"F19.imprint","IMPRINT",FACE,{"disambiguationData":[TD([[makeQuery(id+"F19.imprint","IMPRINT",EDGE,{"derivedFrom":sQuery(id+"F19.wireOp",EDGE,"E178")}),1.0]])]});
            extrude(context, id + "F20", {"entities" : qUnion([Q0]), "depth" : 20 * mm});
        }
    });
